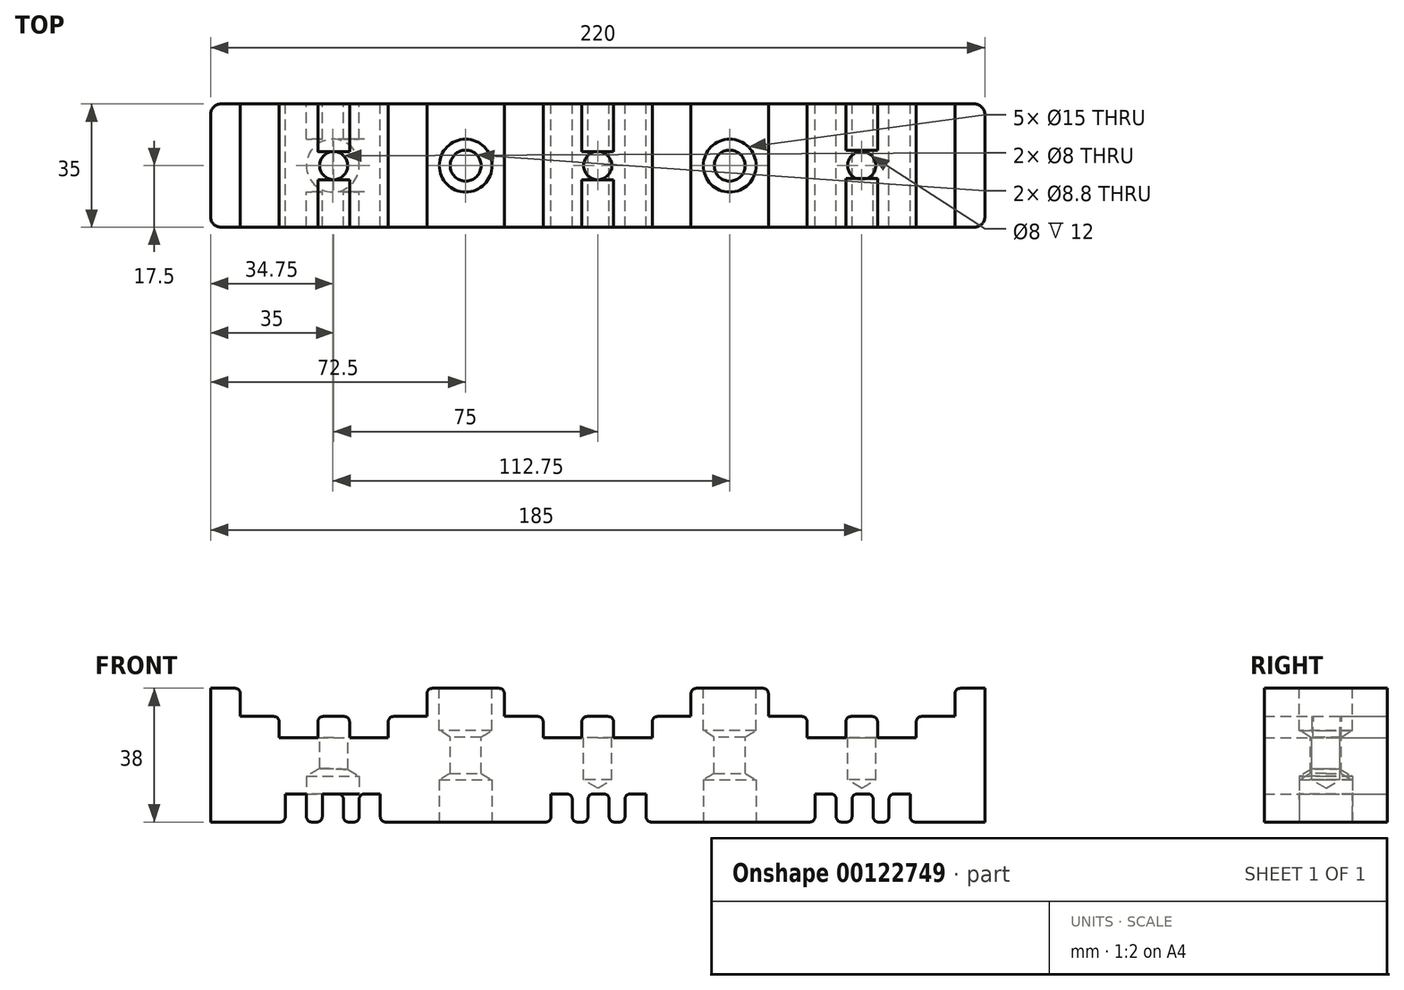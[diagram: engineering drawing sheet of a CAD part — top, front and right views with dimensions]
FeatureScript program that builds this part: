
annotation { "Feature Type Name" : "Feature", "Feature Type Description" : "" }
export const myFeature = defineFeature(function(context is Context, id is Id, definition is map)
    precondition{}
    {
        {
            var Q0;
            Q0=qCreatedBy(makeId("Front.planeOp"),FACE);
            var sketch = newSketch(context, id + "F0", { "sketchPlane" : qUnion([Q0])});
            skLineSegment(sketch, "E0.0", {"start": v(0.5, 5) * mm, "end": v(0.5, 11) * mm});
            skLineSegment(sketch, "E1.0", {"start": v(-10.5, 5) * mm, "end": v(-10.5, 11) * mm});
            skLineSegment(sketch, "E2.0", {"start": v(-21.5, 11) * mm, "end": v(-21.5, 19) * mm});
            skLineSegment(sketch, "E3.MirrorCS", {"start": v(31.5, 11) * mm, "end": v(31.5, 19) * mm});
            skLineSegment(sketch, "E4.MirrorCS", {"start": v(9.5, 5) * mm, "end": v(9.5, 11) * mm});
            skLineSegment(sketch, "E5.MirrorCS", {"start": v(20.5, 5) * mm, "end": v(20.5, 11) * mm});
            skLineSegment(sketch, "E6.trimOffspring", {"start": v(-21.5, 19) * mm, "end": v(-43.5, 19) * mm});
            skLineSegment(sketch, "E7.trimOffspring", {"start": v(0.5, 11) * mm, "end": v(9.5, 11) * mm});
            skLineSegment(sketch, "E8.trimOffspring", {"start": v(20.5, 11) * mm, "end": v(31.5, 11) * mm});
            skLineSegment(sketch, "E9.trimOffspring", {"start": v(-10.5, 5) * mm, "end": v(0.5, 5) * mm});
            skLineSegment(sketch, "E10.trimOffspring", {"start": v(-21.5, 11) * mm, "end": v(-10.5, 11) * mm});
            skLineSegment(sketch, "E11.trimOffspring", {"start": v(9.5, 5) * mm, "end": v(20.5, 5) * mm});
            skLineSegment(sketch, "E12.trimOffspring", {"start": v(53.5, 19) * mm, "end": v(31.5, 19) * mm});
            skLineSegment(sketch, "E13.trimOffspring", {"start": v(-8.25, -19) * mm, "end": v(-56.75, -19) * mm});
            skLineSegment(sketch, "E14.MirrorCS", {"start": v(-62.75, -19) * mm, "end": v(-62.75, -11) * mm});
            skLineSegment(sketch, "E15.MirrorCS", {"start": v(-67.25, -19) * mm, "end": v(-67.25, -11) * mm});
            skLineSegment(sketch, "E16.MirrorCS", {"start": v(-56.75, -19) * mm, "end": v(-56.75, -11) * mm});
            skLineSegment(sketch, "E17.MirrorCS", {"start": v(-67.25, -19) * mm, "end": v(-62.75, -19) * mm});
            skLineSegment(sketch, "E18.trimOffspring", {"start": v(-62.75, -11) * mm, "end": v(-56.75, -11) * mm});
            skLineSegment(sketch, "E19.trimOffspring", {"start": v(-62.75, -19) * mm, "end": v(-67.25, -19) * mm});
            skLineSegment(sketch, "E20", {"start": v(-73.25, -11) * mm, "end": v(-67.25, -11) * mm});
            skLineSegment(sketch, "E21.MirrorCS", {"start": v(-54.5, 5) * mm, "end": v(-54.5, 11) * mm});
            skLineSegment(sketch, "E22.MirrorCS", {"start": v(-43.5, 11) * mm, "end": v(-43.5, 19) * mm});
            skLineSegment(sketch, "E23.MirrorCS", {"start": v(-65.5, 11) * mm, "end": v(-74.5, 11) * mm});
            skLineSegment(sketch, "E24.MirrorCS", {"start": v(-54.5, 5) * mm, "end": v(-65.5, 5) * mm});
            skLineSegment(sketch, "E25.MirrorCS", {"start": v(-65.5, 5) * mm, "end": v(-65.5, 11) * mm});
            skLineSegment(sketch, "E26.MirrorCS", {"start": v(-96.5, 11) * mm, "end": v(-96.5, 19) * mm});
            skLineSegment(sketch, "E27.MirrorCS", {"start": v(-74.5, 5) * mm, "end": v(-74.5, 11) * mm});
            skLineSegment(sketch, "E28.MirrorCS", {"start": v(-85.5, 11) * mm, "end": v(-96.5, 11) * mm});
            skLineSegment(sketch, "E29.MirrorCS", {"start": v(-74.5, 5) * mm, "end": v(-85.5, 5) * mm});
            skLineSegment(sketch, "E30.MirrorCS", {"start": v(-85.5, 5) * mm, "end": v(-85.5, 11) * mm});
            skLineSegment(sketch, "E31.MirrorCS", {"start": v(-43.5, 11) * mm, "end": v(-54.5, 11) * mm});
            skLineSegment(sketch, "E32", {"start": v(-105, 19) * mm, "end": v(-105, -19) * mm});
            skLineSegment(sketch, "E33", {"start": v(-96.5, 19) * mm, "end": v(-105, 19) * mm});
            skLineSegment(sketch, "E34.MirrorCS", {"start": v(-73.25, -19) * mm, "end": v(-77.75, -19) * mm});
            skLineSegment(sketch, "E35.MirrorCS", {"start": v(-73.25, -19) * mm, "end": v(-73.25, -11) * mm});
            skLineSegment(sketch, "E36.MirrorCS", {"start": v(-83.75, -19) * mm, "end": v(-83.75, -11) * mm});
            skLineSegment(sketch, "E37.MirrorCS", {"start": v(-77.75, -19) * mm, "end": v(-73.25, -19) * mm});
            skLineSegment(sketch, "E38.MirrorCS", {"start": v(-77.75, -19) * mm, "end": v(-77.75, -11) * mm});
            skLineSegment(sketch, "E39.MirrorCS", {"start": v(-77.75, -11) * mm, "end": v(-83.75, -11) * mm});
            skLineSegment(sketch, "E40", {"start": v(-83.75, -19) * mm, "end": v(-105, -19) * mm});
            skLineSegment(sketch, "E41.MirrorCS", {"start": v(84.5, 11) * mm, "end": v(75.5, 11) * mm});
            skLineSegment(sketch, "E42.MirrorCS", {"start": v(95.5, 5) * mm, "end": v(84.5, 5) * mm});
            skLineSegment(sketch, "E43.MirrorCS", {"start": v(106.5, 11) * mm, "end": v(106.5, 19) * mm});
            skLineSegment(sketch, "E44.MirrorCS", {"start": v(95.5, 5) * mm, "end": v(95.5, 11) * mm});
            skLineSegment(sketch, "E45.MirrorCS", {"start": v(84.5, 5) * mm, "end": v(84.5, 11) * mm});
            skLineSegment(sketch, "E46.MirrorCS", {"start": v(64.5, 11) * mm, "end": v(53.5, 11) * mm});
            skLineSegment(sketch, "E47.MirrorCS", {"start": v(75.5, 5) * mm, "end": v(75.5, 11) * mm});
            skLineSegment(sketch, "E48.MirrorCS", {"start": v(64.5, 5) * mm, "end": v(64.5, 11) * mm});
            skLineSegment(sketch, "E49.MirrorCS", {"start": v(106.5, 11) * mm, "end": v(95.5, 11) * mm});
            skLineSegment(sketch, "E50.MirrorCS", {"start": v(53.5, 11) * mm, "end": v(53.5, 19) * mm});
            skLineSegment(sketch, "E51.MirrorCS", {"start": v(75.5, 5) * mm, "end": v(64.5, 5) * mm});
            skLineSegment(sketch, "E52.MirrorCS", {"start": v(72.75, -19) * mm, "end": v(77.25, -19) * mm});
            skLineSegment(sketch, "E53.MirrorCS", {"start": v(87.75, -19) * mm, "end": v(83.25, -19) * mm});
            skLineSegment(sketch, "E54.MirrorCS", {"start": v(83.25, -19) * mm, "end": v(87.75, -19) * mm});
            skLineSegment(sketch, "E55.MirrorCS", {"start": v(77.25, -19) * mm, "end": v(72.75, -19) * mm});
            skLineSegment(sketch, "E56.MirrorCS", {"start": v(93.75, -19) * mm, "end": v(93.75, -11) * mm});
            skLineSegment(sketch, "E57.MirrorCS", {"start": v(87.75, -19) * mm, "end": v(87.75, -11) * mm});
            skLineSegment(sketch, "E58.MirrorCS", {"start": v(77.25, -19) * mm, "end": v(77.25, -11) * mm});
            skLineSegment(sketch, "E59.MirrorCS", {"start": v(83.25, -11) * mm, "end": v(77.25, -11) * mm});
            skLineSegment(sketch, "E60.MirrorCS", {"start": v(72.75, -19) * mm, "end": v(72.75, -11) * mm});
            skLineSegment(sketch, "E61.MirrorCS", {"start": v(83.25, -19) * mm, "end": v(83.25, -11) * mm});
            skLineSegment(sketch, "E62.MirrorCS", {"start": v(66.75, -19) * mm, "end": v(66.75, -11) * mm});
            skLineSegment(sketch, "E63.MirrorCS", {"start": v(87.75, -11) * mm, "end": v(93.75, -11) * mm});
            skLineSegment(sketch, "E64.MirrorCS", {"start": v(18.25, -19) * mm, "end": v(66.75, -19) * mm});
            skLineSegment(sketch, "E65.MirrorCS", {"start": v(72.75, -11) * mm, "end": v(66.75, -11) * mm});
            skLineSegment(sketch, "E66.MirrorCS", {"start": v(115, 19) * mm, "end": v(115, -19) * mm});
            skLineSegment(sketch, "E67.MirrorCS", {"start": v(93.75, -19) * mm, "end": v(115, -19) * mm});
            skLineSegment(sketch, "E68.MirrorCS", {"start": v(106.5, 19) * mm, "end": v(115, 19) * mm});
            skLineSegment(sketch, "E69.MirrorCS", {"start": v(-2.25, -19) * mm, "end": v(2.25, -19) * mm});
            skLineSegment(sketch, "E70.MirrorCS", {"start": v(12.75, -19) * mm, "end": v(8.25, -19) * mm});
            skLineSegment(sketch, "E71.MirrorCS", {"start": v(2.25, -19) * mm, "end": v(-2.25, -19) * mm});
            skLineSegment(sketch, "E72.MirrorCS", {"start": v(8.25, -19) * mm, "end": v(12.75, -19) * mm});
            skLineSegment(sketch, "E73.MirrorCS", {"start": v(8.25, -11) * mm, "end": v(2.25, -11) * mm});
            skLineSegment(sketch, "E74.MirrorCS", {"start": v(-8.25, -19) * mm, "end": v(-8.25, -11) * mm});
            skLineSegment(sketch, "E75.MirrorCS", {"start": v(8.25, -19) * mm, "end": v(8.25, -11) * mm});
            skLineSegment(sketch, "E76.MirrorCS", {"start": v(2.25, -19) * mm, "end": v(2.25, -11) * mm});
            skLineSegment(sketch, "E77.MirrorCS", {"start": v(12.75, -19) * mm, "end": v(12.75, -11) * mm});
            skLineSegment(sketch, "E78.MirrorCS", {"start": v(-2.25, -19) * mm, "end": v(-2.25, -11) * mm});
            skLineSegment(sketch, "E79.MirrorCS", {"start": v(18.75, -19) * mm, "end": v(18.75, -11) * mm});
            skLineSegment(sketch, "E80.MirrorCS", {"start": v(-2.25, -11) * mm, "end": v(-8.25, -11) * mm});
            skLineSegment(sketch, "E81.MirrorCS", {"start": v(12.75, -11) * mm, "end": v(18.75, -11) * mm});
            skSolve(sketch);
        }
        {
            var Q0;
            Q0=makeQuery(id+"F0.imprint","IMPRINT",FACE,{"disambiguationData":[TD([[makeQuery(id+"F0.imprint","IMPRINT",EDGE,{"derivedFrom":sQuery(id+"F0.wireOp",EDGE,"qUKRLOlY-Y813-XrE7-N2OE-LMD0eoN4ccjQ.bottom")}),1.0]])]});
            var Q1;
            Q1=makeQuery(id+"F0.imprint","IMPRINT",FACE,{"disambiguationData":[TD([[makeQuery(id+"F0.imprint","IMPRINT",EDGE,{"derivedFrom":sQuery(id+"F0.wireOp",EDGE,"E0.0")}),-1.0]])]});
            extrude(context, id + "F1", {"entities" : qUnion([Q0, Q1]), "endBound" : BoundingType.SYMMETRIC, "depth" : 35 * mm});
        }
        {
            var Q0;
            Q0=makeQuery(id+"F1.opExtrude","SWEPT_FACE",FACE,{"disambiguationData":[OSD([sQuery(id+"F0.wireOp",EDGE,"E6.trimOffspring")])]});
            var sketch = newSketch(context, id + "F2", { "sketchPlane" : qUnion([Q0])});
            skPoint(sketch, "E82", {"position": v(-32.5, 0) * mm});
            skSolve(sketch);
        }
        {
            var Q0;
            Q0=makeQuery(id+"F1.opExtrude","SWEPT_FACE",FACE,{"disambiguationData":[OSD([sQuery(id+"F0.wireOp",EDGE,"E12.trimOffspring")])]});
            var sketch = newSketch(context, id + "F3", { "sketchPlane" : qUnion([Q0])});
            skPoint(sketch, "E83", {"position": v(42.5, 0) * mm});
            skSolve(sketch);
        }
        {
            var Q0;
            Q0=sQuery(id+"F2.wireOp",VERTEX,"E82");
            var Q1;
            Q1=sQuery(id+"F3.wireOp",VERTEX,"E83");
            var Q2;
            Q2=makeQuery(id+"F1.opExtrude","SWEPT_BODY",BODY,{"disambiguationData":[OSD([sQuery(id+"F0.wireOp",EDGE,"qUKRLOlY-Y813-XrE7-N2OE-LMD0eoN4ccjQ.bottom"),sQuery(id+"F0.wireOp",EDGE,"qUKRLOlY-Y813-XrE7-N2OE-LMD0eoN4ccjQ.top"),sQuery(id+"F0.wireOp",EDGE,"qUKRLOlY-Y813-XrE7-N2OE-LMD0eoN4ccjQ.left"),sQuery(id+"F0.wireOp",EDGE,"qUKRLOlY-Y813-XrE7-N2OE-LMD0eoN4ccjQ.right"),sQuery(id+"F0.wireOp",EDGE,"E0.0"),sQuery(id+"F0.wireOp",EDGE,"E1.0"),sQuery(id+"F0.wireOp",EDGE,"E2.0"),sQuery(id+"F0.wireOp",EDGE,"E3.MirrorCS"),sQuery(id+"F0.wireOp",EDGE,"E4.MirrorCS"),sQuery(id+"F0.wireOp",EDGE,"E5.MirrorCS"),sQuery(id+"F0.wireOp",EDGE,"TjQb5iGG-fkCj-vYVZ-Nu9b-291HRNzRSE6Z"),sQuery(id+"F0.wireOp",EDGE,"h24EoQMx-XsVo-RRqw-633f-RRsx9g0fc5Eq"),sQuery(id+"F0.wireOp",EDGE,"E6.trimOffspring"),sQuery(id+"F0.wireOp",EDGE,"E7.trimOffspring"),sQuery(id+"F0.wireOp",EDGE,"E8.trimOffspring"),sQuery(id+"F0.wireOp",EDGE,"8b73c36c-5120-4386-843b-b878e4734d4d1.MirrorCS"),sQuery(id+"F0.wireOp",EDGE,"8b73c36c-5120-4386-843b-b878e4734d4d3.MirrorCS"),sQuery(id+"F0.wireOp",EDGE,"8b73c36c-5120-4386-843b-b878e4734d4d4.MirrorCS"),sQuery(id+"F0.wireOp",EDGE,"8b73c36c-5120-4386-843b-b878e4734d4d5.MirrorCS"),sQuery(id+"F0.wireOp",EDGE,"8b73c36c-5120-4386-843b-b878e4734d4d7.MirrorCS"),sQuery(id+"F0.wireOp",EDGE,"8b73c36c-5120-4386-843b-b878e4734d4d8.MirrorCS"),sQuery(id+"F0.wireOp",EDGE,"65cf6d62-715c-4288-bebc-f9a01cc2506c2.MirrorCS"),sQuery(id+"F0.wireOp",EDGE,"65cf6d62-715c-4288-bebc-f9a01cc2506c3.MirrorCS"),sQuery(id+"F0.wireOp",EDGE,"65cf6d62-715c-4288-bebc-f9a01cc2506c4.MirrorCS"),sQuery(id+"F0.wireOp",EDGE,"65cf6d62-715c-4288-bebc-f9a01cc2506c5.MirrorCS"),sQuery(id+"F0.wireOp",EDGE,"65cf6d62-715c-4288-bebc-f9a01cc2506c6.MirrorCS"),sQuery(id+"F0.wireOp",EDGE,"65cf6d62-715c-4288-bebc-f9a01cc2506c7.MirrorCS"),sQuery(id+"F0.wireOp",EDGE,"4a5b6571-950c-4346-9e1a-99945dc3ca6b.trimOffspring"),sQuery(id+"F0.wireOp",EDGE,"fb7405d8-da36-487f-9ed8-d8622c99c7ee.trimOffspring"),sQuery(id+"F0.wireOp",EDGE,"ab254f91-2f6a-413b-b511-45bfff14a4ab.trimOffspring"),sQuery(id+"F0.wireOp",EDGE,"E9.trimOffspring"),sQuery(id+"F0.wireOp",EDGE,"E10.trimOffspring"),sQuery(id+"F0.wireOp",EDGE,"ce79941b-d8fd-4083-a2b9-c43c18c97298.trimOffspring"),sQuery(id+"F0.wireOp",EDGE,"E11.trimOffspring"),sQuery(id+"F0.wireOp",EDGE,"f32119e2-eb2d-4ad9-8c31-14fa2610f7e9.trimOffspring"),sQuery(id+"F0.wireOp",EDGE,"637628f6-76f3-4957-be79-8dbfd713e1ae.trimOffspring"),sQuery(id+"F0.wireOp",EDGE,"9485339e-7a65-4967-b426-d082cf6546cb.trimOffspring"),sQuery(id+"F0.wireOp",EDGE,"E12.trimOffspring"),sQuery(id+"F0.wireOp",EDGE,"f8046593-27ad-4778-b1d2-df4c1e0aed3c.trimOffspring"),sQuery(id+"F0.wireOp",EDGE,"d27bffa6-3cba-47ef-9795-798ee1ffffde.trimOffspring"),sQuery(id+"F0.wireOp",EDGE,"33a094fa-06ee-4256-bd1e-0f0ed5d178c0.0"),sQuery(id+"F0.wireOp",EDGE,"55134d35-60a4-4e31-8a7f-2c045abbdfaa.0"),sQuery(id+"F0.wireOp",EDGE,"4c2b0ad7-626b-4ce9-a313-3830519edc45.0"),sQuery(id+"F0.wireOp",EDGE,"3a7a6e12-f6d4-474c-8dc6-5767f96f3bfd0.MirrorCS"),sQuery(id+"F0.wireOp",EDGE,"f48c8ded-54f3-4706-a0ea-63bda03a67b5.trimOffspring"),sQuery(id+"F0.wireOp",EDGE,"E13.trimOffspring"),sQuery(id+"F0.wireOp",EDGE,"5ea96fcb-b208-4deb-8b26-572a86056be7.trimOffspring"),sQuery(id+"F0.wireOp",EDGE,"E16.MirrorCS"),sQuery(id+"F0.wireOp",EDGE,"E14.MirrorCS"),sQuery(id+"F0.wireOp",EDGE,"bcb0f907-a76e-4cdd-baca-5b1385e896aa2.MirrorCS"),sQuery(id+"F0.wireOp",EDGE,"E15.MirrorCS"),sQuery(id+"F0.wireOp",EDGE,"f6293f27-9fd1-40ac-aa67-5afb52735e2d0.MirrorCS"),sQuery(id+"F0.wireOp",EDGE,"f6293f27-9fd1-40ac-aa67-5afb52735e2d1.MirrorCS"),sQuery(id+"F0.wireOp",EDGE,"f6293f27-9fd1-40ac-aa67-5afb52735e2d3.MirrorCS"),sQuery(id+"F0.wireOp",EDGE,"f6293f27-9fd1-40ac-aa67-5afb52735e2d4.MirrorCS"),sQuery(id+"F0.wireOp",EDGE,"E18.trimOffspring"),sQuery(id+"F0.wireOp",EDGE,"E19.trimOffspring"),sQuery(id+"F0.wireOp",EDGE,"32ee123d-ca43-4cc0-928d-7201b603e702.trimOffspring"),sQuery(id+"F0.wireOp",EDGE,"E20"),sQuery(id+"F0.wireOp",EDGE,"5dcb935a-820c-4198-b4b2-0413f3b87393.trimOffspring"),sQuery(id+"F0.wireOp",EDGE,"7ee461ee-1d67-4faf-a147-f0287e78c71f.trimOffspring"),sQuery(id+"F0.wireOp",EDGE,"189ced0a-a9e9-466e-9166-4b62e1055adb.trimOffspring"),sQuery(id+"F0.wireOp",EDGE,"068751d8-bdd8-45ca-a637-cfe0f5a2bb4a.trimOffspring"),sQuery(id+"F0.wireOp",EDGE,"a825891d-b700-4e83-942a-2eee88b86e3d.trimOffspring")])]});
            hole(context, id + "F4", {"style" : HoleStyle.SIMPLE, "endStyle" : HoleEndStyle.THROUGH, "standardTappedOrClearance" : lookupTablePath({ "standard" : "ISO", "fit" : "Normal", "size" : "M8", "type" : "Clearance" }), "standardBlindInLast" : lookupTablePath({ "fit" : "Standard", "standard" : "ISO", "size" : "M8", "type" : "Clearance" }), "holeDiameter" : 8.8 * mm, "startFromSketch" : true, "locations" : qUnion([Q0, Q1]), "scope" : qUnion([Q2]), "isTappedThrough" : true});
        }
        {
            var Q0;
            Q0=makeQuery(id+"F1.opExtrude","SWEPT_FACE",FACE,{"disambiguationData":[OSD([sQuery(id+"F0.wireOp",EDGE,"E6.trimOffspring")])]});
            var sketch = newSketch(context, id + "F5", { "sketchPlane" : qUnion([Q0])});
            skPoint(sketch, "E84", {"position": v(-32.5, 0) * mm});
            skSolve(sketch);
        }
        {
            var Q0;
            Q0=makeQuery(id+"F1.opExtrude","SWEPT_FACE",FACE,{"disambiguationData":[OSD([sQuery(id+"F0.wireOp",EDGE,"E12.trimOffspring")])]});
            var sketch = newSketch(context, id + "F6", { "sketchPlane" : qUnion([Q0])});
            skPoint(sketch, "E85", {"position": v(42.5, 0) * mm});
            skSolve(sketch);
        }
        {
            var Q0;
            Q0=sQuery(id+"F5.wireOp",VERTEX,"E84");
            var Q1;
            Q1=makeQuery(id+"F1.opExtrude","SWEPT_BODY",BODY,{"disambiguationData":[OSD([sQuery(id+"F0.wireOp",EDGE,"qUKRLOlY-Y813-XrE7-N2OE-LMD0eoN4ccjQ.bottom"),sQuery(id+"F0.wireOp",EDGE,"qUKRLOlY-Y813-XrE7-N2OE-LMD0eoN4ccjQ.top"),sQuery(id+"F0.wireOp",EDGE,"qUKRLOlY-Y813-XrE7-N2OE-LMD0eoN4ccjQ.left"),sQuery(id+"F0.wireOp",EDGE,"qUKRLOlY-Y813-XrE7-N2OE-LMD0eoN4ccjQ.right"),sQuery(id+"F0.wireOp",EDGE,"E0.0"),sQuery(id+"F0.wireOp",EDGE,"E1.0"),sQuery(id+"F0.wireOp",EDGE,"E2.0"),sQuery(id+"F0.wireOp",EDGE,"E3.MirrorCS"),sQuery(id+"F0.wireOp",EDGE,"E4.MirrorCS"),sQuery(id+"F0.wireOp",EDGE,"E5.MirrorCS"),sQuery(id+"F0.wireOp",EDGE,"TjQb5iGG-fkCj-vYVZ-Nu9b-291HRNzRSE6Z"),sQuery(id+"F0.wireOp",EDGE,"h24EoQMx-XsVo-RRqw-633f-RRsx9g0fc5Eq"),sQuery(id+"F0.wireOp",EDGE,"E6.trimOffspring"),sQuery(id+"F0.wireOp",EDGE,"E7.trimOffspring"),sQuery(id+"F0.wireOp",EDGE,"E8.trimOffspring"),sQuery(id+"F0.wireOp",EDGE,"8b73c36c-5120-4386-843b-b878e4734d4d1.MirrorCS"),sQuery(id+"F0.wireOp",EDGE,"8b73c36c-5120-4386-843b-b878e4734d4d3.MirrorCS"),sQuery(id+"F0.wireOp",EDGE,"8b73c36c-5120-4386-843b-b878e4734d4d4.MirrorCS"),sQuery(id+"F0.wireOp",EDGE,"8b73c36c-5120-4386-843b-b878e4734d4d5.MirrorCS"),sQuery(id+"F0.wireOp",EDGE,"8b73c36c-5120-4386-843b-b878e4734d4d7.MirrorCS"),sQuery(id+"F0.wireOp",EDGE,"8b73c36c-5120-4386-843b-b878e4734d4d8.MirrorCS"),sQuery(id+"F0.wireOp",EDGE,"65cf6d62-715c-4288-bebc-f9a01cc2506c2.MirrorCS"),sQuery(id+"F0.wireOp",EDGE,"65cf6d62-715c-4288-bebc-f9a01cc2506c3.MirrorCS"),sQuery(id+"F0.wireOp",EDGE,"65cf6d62-715c-4288-bebc-f9a01cc2506c4.MirrorCS"),sQuery(id+"F0.wireOp",EDGE,"65cf6d62-715c-4288-bebc-f9a01cc2506c5.MirrorCS"),sQuery(id+"F0.wireOp",EDGE,"65cf6d62-715c-4288-bebc-f9a01cc2506c6.MirrorCS"),sQuery(id+"F0.wireOp",EDGE,"65cf6d62-715c-4288-bebc-f9a01cc2506c7.MirrorCS"),sQuery(id+"F0.wireOp",EDGE,"4a5b6571-950c-4346-9e1a-99945dc3ca6b.trimOffspring"),sQuery(id+"F0.wireOp",EDGE,"fb7405d8-da36-487f-9ed8-d8622c99c7ee.trimOffspring"),sQuery(id+"F0.wireOp",EDGE,"ab254f91-2f6a-413b-b511-45bfff14a4ab.trimOffspring"),sQuery(id+"F0.wireOp",EDGE,"E9.trimOffspring"),sQuery(id+"F0.wireOp",EDGE,"E10.trimOffspring"),sQuery(id+"F0.wireOp",EDGE,"ce79941b-d8fd-4083-a2b9-c43c18c97298.trimOffspring"),sQuery(id+"F0.wireOp",EDGE,"E11.trimOffspring"),sQuery(id+"F0.wireOp",EDGE,"f32119e2-eb2d-4ad9-8c31-14fa2610f7e9.trimOffspring"),sQuery(id+"F0.wireOp",EDGE,"637628f6-76f3-4957-be79-8dbfd713e1ae.trimOffspring"),sQuery(id+"F0.wireOp",EDGE,"9485339e-7a65-4967-b426-d082cf6546cb.trimOffspring"),sQuery(id+"F0.wireOp",EDGE,"E12.trimOffspring"),sQuery(id+"F0.wireOp",EDGE,"f8046593-27ad-4778-b1d2-df4c1e0aed3c.trimOffspring"),sQuery(id+"F0.wireOp",EDGE,"d27bffa6-3cba-47ef-9795-798ee1ffffde.trimOffspring"),sQuery(id+"F0.wireOp",EDGE,"33a094fa-06ee-4256-bd1e-0f0ed5d178c0.0"),sQuery(id+"F0.wireOp",EDGE,"55134d35-60a4-4e31-8a7f-2c045abbdfaa.0"),sQuery(id+"F0.wireOp",EDGE,"4c2b0ad7-626b-4ce9-a313-3830519edc45.0"),sQuery(id+"F0.wireOp",EDGE,"3a7a6e12-f6d4-474c-8dc6-5767f96f3bfd0.MirrorCS"),sQuery(id+"F0.wireOp",EDGE,"f48c8ded-54f3-4706-a0ea-63bda03a67b5.trimOffspring"),sQuery(id+"F0.wireOp",EDGE,"E13.trimOffspring"),sQuery(id+"F0.wireOp",EDGE,"5ea96fcb-b208-4deb-8b26-572a86056be7.trimOffspring"),sQuery(id+"F0.wireOp",EDGE,"E16.MirrorCS"),sQuery(id+"F0.wireOp",EDGE,"E14.MirrorCS"),sQuery(id+"F0.wireOp",EDGE,"bcb0f907-a76e-4cdd-baca-5b1385e896aa2.MirrorCS"),sQuery(id+"F0.wireOp",EDGE,"E15.MirrorCS"),sQuery(id+"F0.wireOp",EDGE,"f6293f27-9fd1-40ac-aa67-5afb52735e2d0.MirrorCS"),sQuery(id+"F0.wireOp",EDGE,"f6293f27-9fd1-40ac-aa67-5afb52735e2d1.MirrorCS"),sQuery(id+"F0.wireOp",EDGE,"f6293f27-9fd1-40ac-aa67-5afb52735e2d3.MirrorCS"),sQuery(id+"F0.wireOp",EDGE,"f6293f27-9fd1-40ac-aa67-5afb52735e2d4.MirrorCS"),sQuery(id+"F0.wireOp",EDGE,"E18.trimOffspring"),sQuery(id+"F0.wireOp",EDGE,"E19.trimOffspring"),sQuery(id+"F0.wireOp",EDGE,"32ee123d-ca43-4cc0-928d-7201b603e702.trimOffspring"),sQuery(id+"F0.wireOp",EDGE,"E20"),sQuery(id+"F0.wireOp",EDGE,"5dcb935a-820c-4198-b4b2-0413f3b87393.trimOffspring"),sQuery(id+"F0.wireOp",EDGE,"7ee461ee-1d67-4faf-a147-f0287e78c71f.trimOffspring"),sQuery(id+"F0.wireOp",EDGE,"189ced0a-a9e9-466e-9166-4b62e1055adb.trimOffspring"),sQuery(id+"F0.wireOp",EDGE,"068751d8-bdd8-45ca-a637-cfe0f5a2bb4a.trimOffspring"),sQuery(id+"F0.wireOp",EDGE,"a825891d-b700-4e83-942a-2eee88b86e3d.trimOffspring")])]});
            hole(context, id + "F7", {"style" : HoleStyle.SIMPLE, "endStyle" : HoleEndStyle.BLIND, "holeDiameter" : 15 * mm, "holeDepth" : 12 * mm, "startFromSketch" : true, "locations" : qUnion([Q0]), "scope" : qUnion([Q1])});
        }
        {
            var Q0;
            Q0=sQuery(id+"F6.wireOp",VERTEX,"E85");
            var Q1;
            Q1=makeQuery(id+"F1.opExtrude","SWEPT_BODY",BODY,{"disambiguationData":[OSD([sQuery(id+"F0.wireOp",EDGE,"qUKRLOlY-Y813-XrE7-N2OE-LMD0eoN4ccjQ.bottom"),sQuery(id+"F0.wireOp",EDGE,"qUKRLOlY-Y813-XrE7-N2OE-LMD0eoN4ccjQ.top"),sQuery(id+"F0.wireOp",EDGE,"qUKRLOlY-Y813-XrE7-N2OE-LMD0eoN4ccjQ.left"),sQuery(id+"F0.wireOp",EDGE,"qUKRLOlY-Y813-XrE7-N2OE-LMD0eoN4ccjQ.right"),sQuery(id+"F0.wireOp",EDGE,"E0.0"),sQuery(id+"F0.wireOp",EDGE,"E1.0"),sQuery(id+"F0.wireOp",EDGE,"E2.0"),sQuery(id+"F0.wireOp",EDGE,"E3.MirrorCS"),sQuery(id+"F0.wireOp",EDGE,"E4.MirrorCS"),sQuery(id+"F0.wireOp",EDGE,"E5.MirrorCS"),sQuery(id+"F0.wireOp",EDGE,"TjQb5iGG-fkCj-vYVZ-Nu9b-291HRNzRSE6Z"),sQuery(id+"F0.wireOp",EDGE,"h24EoQMx-XsVo-RRqw-633f-RRsx9g0fc5Eq"),sQuery(id+"F0.wireOp",EDGE,"E6.trimOffspring"),sQuery(id+"F0.wireOp",EDGE,"E7.trimOffspring"),sQuery(id+"F0.wireOp",EDGE,"E8.trimOffspring"),sQuery(id+"F0.wireOp",EDGE,"8b73c36c-5120-4386-843b-b878e4734d4d1.MirrorCS"),sQuery(id+"F0.wireOp",EDGE,"8b73c36c-5120-4386-843b-b878e4734d4d3.MirrorCS"),sQuery(id+"F0.wireOp",EDGE,"8b73c36c-5120-4386-843b-b878e4734d4d4.MirrorCS"),sQuery(id+"F0.wireOp",EDGE,"8b73c36c-5120-4386-843b-b878e4734d4d5.MirrorCS"),sQuery(id+"F0.wireOp",EDGE,"8b73c36c-5120-4386-843b-b878e4734d4d7.MirrorCS"),sQuery(id+"F0.wireOp",EDGE,"8b73c36c-5120-4386-843b-b878e4734d4d8.MirrorCS"),sQuery(id+"F0.wireOp",EDGE,"65cf6d62-715c-4288-bebc-f9a01cc2506c2.MirrorCS"),sQuery(id+"F0.wireOp",EDGE,"65cf6d62-715c-4288-bebc-f9a01cc2506c3.MirrorCS"),sQuery(id+"F0.wireOp",EDGE,"65cf6d62-715c-4288-bebc-f9a01cc2506c4.MirrorCS"),sQuery(id+"F0.wireOp",EDGE,"65cf6d62-715c-4288-bebc-f9a01cc2506c5.MirrorCS"),sQuery(id+"F0.wireOp",EDGE,"65cf6d62-715c-4288-bebc-f9a01cc2506c6.MirrorCS"),sQuery(id+"F0.wireOp",EDGE,"65cf6d62-715c-4288-bebc-f9a01cc2506c7.MirrorCS"),sQuery(id+"F0.wireOp",EDGE,"4a5b6571-950c-4346-9e1a-99945dc3ca6b.trimOffspring"),sQuery(id+"F0.wireOp",EDGE,"fb7405d8-da36-487f-9ed8-d8622c99c7ee.trimOffspring"),sQuery(id+"F0.wireOp",EDGE,"ab254f91-2f6a-413b-b511-45bfff14a4ab.trimOffspring"),sQuery(id+"F0.wireOp",EDGE,"E9.trimOffspring"),sQuery(id+"F0.wireOp",EDGE,"E10.trimOffspring"),sQuery(id+"F0.wireOp",EDGE,"ce79941b-d8fd-4083-a2b9-c43c18c97298.trimOffspring"),sQuery(id+"F0.wireOp",EDGE,"E11.trimOffspring"),sQuery(id+"F0.wireOp",EDGE,"f32119e2-eb2d-4ad9-8c31-14fa2610f7e9.trimOffspring"),sQuery(id+"F0.wireOp",EDGE,"637628f6-76f3-4957-be79-8dbfd713e1ae.trimOffspring"),sQuery(id+"F0.wireOp",EDGE,"9485339e-7a65-4967-b426-d082cf6546cb.trimOffspring"),sQuery(id+"F0.wireOp",EDGE,"E12.trimOffspring"),sQuery(id+"F0.wireOp",EDGE,"f8046593-27ad-4778-b1d2-df4c1e0aed3c.trimOffspring"),sQuery(id+"F0.wireOp",EDGE,"d27bffa6-3cba-47ef-9795-798ee1ffffde.trimOffspring"),sQuery(id+"F0.wireOp",EDGE,"33a094fa-06ee-4256-bd1e-0f0ed5d178c0.0"),sQuery(id+"F0.wireOp",EDGE,"55134d35-60a4-4e31-8a7f-2c045abbdfaa.0"),sQuery(id+"F0.wireOp",EDGE,"4c2b0ad7-626b-4ce9-a313-3830519edc45.0"),sQuery(id+"F0.wireOp",EDGE,"3a7a6e12-f6d4-474c-8dc6-5767f96f3bfd0.MirrorCS"),sQuery(id+"F0.wireOp",EDGE,"f48c8ded-54f3-4706-a0ea-63bda03a67b5.trimOffspring"),sQuery(id+"F0.wireOp",EDGE,"E13.trimOffspring"),sQuery(id+"F0.wireOp",EDGE,"5ea96fcb-b208-4deb-8b26-572a86056be7.trimOffspring"),sQuery(id+"F0.wireOp",EDGE,"E16.MirrorCS"),sQuery(id+"F0.wireOp",EDGE,"E14.MirrorCS"),sQuery(id+"F0.wireOp",EDGE,"bcb0f907-a76e-4cdd-baca-5b1385e896aa2.MirrorCS"),sQuery(id+"F0.wireOp",EDGE,"E15.MirrorCS"),sQuery(id+"F0.wireOp",EDGE,"f6293f27-9fd1-40ac-aa67-5afb52735e2d0.MirrorCS"),sQuery(id+"F0.wireOp",EDGE,"f6293f27-9fd1-40ac-aa67-5afb52735e2d1.MirrorCS"),sQuery(id+"F0.wireOp",EDGE,"f6293f27-9fd1-40ac-aa67-5afb52735e2d3.MirrorCS"),sQuery(id+"F0.wireOp",EDGE,"f6293f27-9fd1-40ac-aa67-5afb52735e2d4.MirrorCS"),sQuery(id+"F0.wireOp",EDGE,"E18.trimOffspring"),sQuery(id+"F0.wireOp",EDGE,"E19.trimOffspring"),sQuery(id+"F0.wireOp",EDGE,"32ee123d-ca43-4cc0-928d-7201b603e702.trimOffspring"),sQuery(id+"F0.wireOp",EDGE,"E20"),sQuery(id+"F0.wireOp",EDGE,"5dcb935a-820c-4198-b4b2-0413f3b87393.trimOffspring"),sQuery(id+"F0.wireOp",EDGE,"7ee461ee-1d67-4faf-a147-f0287e78c71f.trimOffspring"),sQuery(id+"F0.wireOp",EDGE,"189ced0a-a9e9-466e-9166-4b62e1055adb.trimOffspring"),sQuery(id+"F0.wireOp",EDGE,"068751d8-bdd8-45ca-a637-cfe0f5a2bb4a.trimOffspring"),sQuery(id+"F0.wireOp",EDGE,"a825891d-b700-4e83-942a-2eee88b86e3d.trimOffspring")])]});
            hole(context, id + "F8", {"style" : HoleStyle.SIMPLE, "endStyle" : HoleEndStyle.BLIND, "holeDiameter" : 15 * mm, "holeDepth" : 12 * mm, "startFromSketch" : true, "locations" : qUnion([Q0]), "scope" : qUnion([Q1])});
        }
        {
            var Q0;
            Q0=makeQuery(id+"F1.opExtrude","SWEPT_FACE",FACE,{"disambiguationData":[OSD([sQuery(id+"F0.wireOp",EDGE,"E64.MirrorCS")])]});
            var sketch = newSketch(context, id + "F9", { "sketchPlane" : qUnion([Q0])});
            skPoint(sketch, "E86", {"position": v(42.5, 0) * mm});
            skSolve(sketch);
        }
        {
            var Q0;
            Q0=makeQuery(id+"F1.opExtrude","SWEPT_FACE",FACE,{"disambiguationData":[OSD([sQuery(id+"F0.wireOp",EDGE,"E13.trimOffspring")])]});
            var sketch = newSketch(context, id + "F10", { "sketchPlane" : qUnion([Q0])});
            skPoint(sketch, "E87", {"position": v(-32.5, 0) * mm});
            skSolve(sketch);
        }
        {
            var Q0;
            Q0=sQuery(id+"F9.wireOp",VERTEX,"E86");
            var Q1;
            Q1=makeQuery(id+"F1.opExtrude","SWEPT_BODY",BODY,{"disambiguationData":[OSD([sQuery(id+"F0.wireOp",EDGE,"qUKRLOlY-Y813-XrE7-N2OE-LMD0eoN4ccjQ.bottom"),sQuery(id+"F0.wireOp",EDGE,"qUKRLOlY-Y813-XrE7-N2OE-LMD0eoN4ccjQ.top"),sQuery(id+"F0.wireOp",EDGE,"qUKRLOlY-Y813-XrE7-N2OE-LMD0eoN4ccjQ.left"),sQuery(id+"F0.wireOp",EDGE,"qUKRLOlY-Y813-XrE7-N2OE-LMD0eoN4ccjQ.right"),sQuery(id+"F0.wireOp",EDGE,"E0.0"),sQuery(id+"F0.wireOp",EDGE,"E1.0"),sQuery(id+"F0.wireOp",EDGE,"E2.0"),sQuery(id+"F0.wireOp",EDGE,"E3.MirrorCS"),sQuery(id+"F0.wireOp",EDGE,"E4.MirrorCS"),sQuery(id+"F0.wireOp",EDGE,"E5.MirrorCS"),sQuery(id+"F0.wireOp",EDGE,"TjQb5iGG-fkCj-vYVZ-Nu9b-291HRNzRSE6Z"),sQuery(id+"F0.wireOp",EDGE,"h24EoQMx-XsVo-RRqw-633f-RRsx9g0fc5Eq"),sQuery(id+"F0.wireOp",EDGE,"E6.trimOffspring"),sQuery(id+"F0.wireOp",EDGE,"E7.trimOffspring"),sQuery(id+"F0.wireOp",EDGE,"E8.trimOffspring"),sQuery(id+"F0.wireOp",EDGE,"8b73c36c-5120-4386-843b-b878e4734d4d1.MirrorCS"),sQuery(id+"F0.wireOp",EDGE,"8b73c36c-5120-4386-843b-b878e4734d4d3.MirrorCS"),sQuery(id+"F0.wireOp",EDGE,"8b73c36c-5120-4386-843b-b878e4734d4d4.MirrorCS"),sQuery(id+"F0.wireOp",EDGE,"8b73c36c-5120-4386-843b-b878e4734d4d5.MirrorCS"),sQuery(id+"F0.wireOp",EDGE,"8b73c36c-5120-4386-843b-b878e4734d4d7.MirrorCS"),sQuery(id+"F0.wireOp",EDGE,"8b73c36c-5120-4386-843b-b878e4734d4d8.MirrorCS"),sQuery(id+"F0.wireOp",EDGE,"65cf6d62-715c-4288-bebc-f9a01cc2506c2.MirrorCS"),sQuery(id+"F0.wireOp",EDGE,"65cf6d62-715c-4288-bebc-f9a01cc2506c3.MirrorCS"),sQuery(id+"F0.wireOp",EDGE,"65cf6d62-715c-4288-bebc-f9a01cc2506c4.MirrorCS"),sQuery(id+"F0.wireOp",EDGE,"65cf6d62-715c-4288-bebc-f9a01cc2506c5.MirrorCS"),sQuery(id+"F0.wireOp",EDGE,"65cf6d62-715c-4288-bebc-f9a01cc2506c6.MirrorCS"),sQuery(id+"F0.wireOp",EDGE,"65cf6d62-715c-4288-bebc-f9a01cc2506c7.MirrorCS"),sQuery(id+"F0.wireOp",EDGE,"4a5b6571-950c-4346-9e1a-99945dc3ca6b.trimOffspring"),sQuery(id+"F0.wireOp",EDGE,"fb7405d8-da36-487f-9ed8-d8622c99c7ee.trimOffspring"),sQuery(id+"F0.wireOp",EDGE,"ab254f91-2f6a-413b-b511-45bfff14a4ab.trimOffspring"),sQuery(id+"F0.wireOp",EDGE,"E9.trimOffspring"),sQuery(id+"F0.wireOp",EDGE,"E10.trimOffspring"),sQuery(id+"F0.wireOp",EDGE,"ce79941b-d8fd-4083-a2b9-c43c18c97298.trimOffspring"),sQuery(id+"F0.wireOp",EDGE,"E11.trimOffspring"),sQuery(id+"F0.wireOp",EDGE,"f32119e2-eb2d-4ad9-8c31-14fa2610f7e9.trimOffspring"),sQuery(id+"F0.wireOp",EDGE,"637628f6-76f3-4957-be79-8dbfd713e1ae.trimOffspring"),sQuery(id+"F0.wireOp",EDGE,"9485339e-7a65-4967-b426-d082cf6546cb.trimOffspring"),sQuery(id+"F0.wireOp",EDGE,"E12.trimOffspring"),sQuery(id+"F0.wireOp",EDGE,"f8046593-27ad-4778-b1d2-df4c1e0aed3c.trimOffspring"),sQuery(id+"F0.wireOp",EDGE,"d27bffa6-3cba-47ef-9795-798ee1ffffde.trimOffspring"),sQuery(id+"F0.wireOp",EDGE,"33a094fa-06ee-4256-bd1e-0f0ed5d178c0.0"),sQuery(id+"F0.wireOp",EDGE,"55134d35-60a4-4e31-8a7f-2c045abbdfaa.0"),sQuery(id+"F0.wireOp",EDGE,"4c2b0ad7-626b-4ce9-a313-3830519edc45.0"),sQuery(id+"F0.wireOp",EDGE,"3a7a6e12-f6d4-474c-8dc6-5767f96f3bfd0.MirrorCS"),sQuery(id+"F0.wireOp",EDGE,"f48c8ded-54f3-4706-a0ea-63bda03a67b5.trimOffspring"),sQuery(id+"F0.wireOp",EDGE,"E13.trimOffspring"),sQuery(id+"F0.wireOp",EDGE,"5ea96fcb-b208-4deb-8b26-572a86056be7.trimOffspring"),sQuery(id+"F0.wireOp",EDGE,"E16.MirrorCS"),sQuery(id+"F0.wireOp",EDGE,"E14.MirrorCS"),sQuery(id+"F0.wireOp",EDGE,"bcb0f907-a76e-4cdd-baca-5b1385e896aa2.MirrorCS"),sQuery(id+"F0.wireOp",EDGE,"E15.MirrorCS"),sQuery(id+"F0.wireOp",EDGE,"f6293f27-9fd1-40ac-aa67-5afb52735e2d0.MirrorCS"),sQuery(id+"F0.wireOp",EDGE,"f6293f27-9fd1-40ac-aa67-5afb52735e2d1.MirrorCS"),sQuery(id+"F0.wireOp",EDGE,"f6293f27-9fd1-40ac-aa67-5afb52735e2d3.MirrorCS"),sQuery(id+"F0.wireOp",EDGE,"f6293f27-9fd1-40ac-aa67-5afb52735e2d4.MirrorCS"),sQuery(id+"F0.wireOp",EDGE,"E18.trimOffspring"),sQuery(id+"F0.wireOp",EDGE,"E19.trimOffspring"),sQuery(id+"F0.wireOp",EDGE,"32ee123d-ca43-4cc0-928d-7201b603e702.trimOffspring"),sQuery(id+"F0.wireOp",EDGE,"E20"),sQuery(id+"F0.wireOp",EDGE,"5dcb935a-820c-4198-b4b2-0413f3b87393.trimOffspring"),sQuery(id+"F0.wireOp",EDGE,"7ee461ee-1d67-4faf-a147-f0287e78c71f.trimOffspring"),sQuery(id+"F0.wireOp",EDGE,"189ced0a-a9e9-466e-9166-4b62e1055adb.trimOffspring"),sQuery(id+"F0.wireOp",EDGE,"068751d8-bdd8-45ca-a637-cfe0f5a2bb4a.trimOffspring"),sQuery(id+"F0.wireOp",EDGE,"a825891d-b700-4e83-942a-2eee88b86e3d.trimOffspring")])]});
            hole(context, id + "F11", {"style" : HoleStyle.SIMPLE, "endStyle" : HoleEndStyle.BLIND, "holeDiameter" : 15 * mm, "holeDepth" : 12 * mm, "startFromSketch" : true, "locations" : qUnion([Q0]), "scope" : qUnion([Q1])});
        }
        {
            var Q0;
            Q0=sQuery(id+"F10.wireOp",VERTEX,"E87");
            var Q1;
            Q1=makeQuery(id+"F1.opExtrude","SWEPT_BODY",BODY,{"disambiguationData":[OSD([sQuery(id+"F0.wireOp",EDGE,"qUKRLOlY-Y813-XrE7-N2OE-LMD0eoN4ccjQ.bottom"),sQuery(id+"F0.wireOp",EDGE,"qUKRLOlY-Y813-XrE7-N2OE-LMD0eoN4ccjQ.top"),sQuery(id+"F0.wireOp",EDGE,"qUKRLOlY-Y813-XrE7-N2OE-LMD0eoN4ccjQ.left"),sQuery(id+"F0.wireOp",EDGE,"qUKRLOlY-Y813-XrE7-N2OE-LMD0eoN4ccjQ.right"),sQuery(id+"F0.wireOp",EDGE,"E0.0"),sQuery(id+"F0.wireOp",EDGE,"E1.0"),sQuery(id+"F0.wireOp",EDGE,"E2.0"),sQuery(id+"F0.wireOp",EDGE,"E3.MirrorCS"),sQuery(id+"F0.wireOp",EDGE,"E4.MirrorCS"),sQuery(id+"F0.wireOp",EDGE,"E5.MirrorCS"),sQuery(id+"F0.wireOp",EDGE,"TjQb5iGG-fkCj-vYVZ-Nu9b-291HRNzRSE6Z"),sQuery(id+"F0.wireOp",EDGE,"h24EoQMx-XsVo-RRqw-633f-RRsx9g0fc5Eq"),sQuery(id+"F0.wireOp",EDGE,"E6.trimOffspring"),sQuery(id+"F0.wireOp",EDGE,"E7.trimOffspring"),sQuery(id+"F0.wireOp",EDGE,"E8.trimOffspring"),sQuery(id+"F0.wireOp",EDGE,"8b73c36c-5120-4386-843b-b878e4734d4d1.MirrorCS"),sQuery(id+"F0.wireOp",EDGE,"8b73c36c-5120-4386-843b-b878e4734d4d3.MirrorCS"),sQuery(id+"F0.wireOp",EDGE,"8b73c36c-5120-4386-843b-b878e4734d4d4.MirrorCS"),sQuery(id+"F0.wireOp",EDGE,"8b73c36c-5120-4386-843b-b878e4734d4d5.MirrorCS"),sQuery(id+"F0.wireOp",EDGE,"8b73c36c-5120-4386-843b-b878e4734d4d7.MirrorCS"),sQuery(id+"F0.wireOp",EDGE,"8b73c36c-5120-4386-843b-b878e4734d4d8.MirrorCS"),sQuery(id+"F0.wireOp",EDGE,"65cf6d62-715c-4288-bebc-f9a01cc2506c2.MirrorCS"),sQuery(id+"F0.wireOp",EDGE,"65cf6d62-715c-4288-bebc-f9a01cc2506c3.MirrorCS"),sQuery(id+"F0.wireOp",EDGE,"65cf6d62-715c-4288-bebc-f9a01cc2506c4.MirrorCS"),sQuery(id+"F0.wireOp",EDGE,"65cf6d62-715c-4288-bebc-f9a01cc2506c5.MirrorCS"),sQuery(id+"F0.wireOp",EDGE,"65cf6d62-715c-4288-bebc-f9a01cc2506c6.MirrorCS"),sQuery(id+"F0.wireOp",EDGE,"65cf6d62-715c-4288-bebc-f9a01cc2506c7.MirrorCS"),sQuery(id+"F0.wireOp",EDGE,"4a5b6571-950c-4346-9e1a-99945dc3ca6b.trimOffspring"),sQuery(id+"F0.wireOp",EDGE,"fb7405d8-da36-487f-9ed8-d8622c99c7ee.trimOffspring"),sQuery(id+"F0.wireOp",EDGE,"ab254f91-2f6a-413b-b511-45bfff14a4ab.trimOffspring"),sQuery(id+"F0.wireOp",EDGE,"E9.trimOffspring"),sQuery(id+"F0.wireOp",EDGE,"E10.trimOffspring"),sQuery(id+"F0.wireOp",EDGE,"ce79941b-d8fd-4083-a2b9-c43c18c97298.trimOffspring"),sQuery(id+"F0.wireOp",EDGE,"E11.trimOffspring"),sQuery(id+"F0.wireOp",EDGE,"f32119e2-eb2d-4ad9-8c31-14fa2610f7e9.trimOffspring"),sQuery(id+"F0.wireOp",EDGE,"637628f6-76f3-4957-be79-8dbfd713e1ae.trimOffspring"),sQuery(id+"F0.wireOp",EDGE,"9485339e-7a65-4967-b426-d082cf6546cb.trimOffspring"),sQuery(id+"F0.wireOp",EDGE,"E12.trimOffspring"),sQuery(id+"F0.wireOp",EDGE,"f8046593-27ad-4778-b1d2-df4c1e0aed3c.trimOffspring"),sQuery(id+"F0.wireOp",EDGE,"d27bffa6-3cba-47ef-9795-798ee1ffffde.trimOffspring"),sQuery(id+"F0.wireOp",EDGE,"33a094fa-06ee-4256-bd1e-0f0ed5d178c0.0"),sQuery(id+"F0.wireOp",EDGE,"55134d35-60a4-4e31-8a7f-2c045abbdfaa.0"),sQuery(id+"F0.wireOp",EDGE,"4c2b0ad7-626b-4ce9-a313-3830519edc45.0"),sQuery(id+"F0.wireOp",EDGE,"3a7a6e12-f6d4-474c-8dc6-5767f96f3bfd0.MirrorCS"),sQuery(id+"F0.wireOp",EDGE,"f48c8ded-54f3-4706-a0ea-63bda03a67b5.trimOffspring"),sQuery(id+"F0.wireOp",EDGE,"E13.trimOffspring"),sQuery(id+"F0.wireOp",EDGE,"5ea96fcb-b208-4deb-8b26-572a86056be7.trimOffspring"),sQuery(id+"F0.wireOp",EDGE,"E16.MirrorCS"),sQuery(id+"F0.wireOp",EDGE,"E14.MirrorCS"),sQuery(id+"F0.wireOp",EDGE,"bcb0f907-a76e-4cdd-baca-5b1385e896aa2.MirrorCS"),sQuery(id+"F0.wireOp",EDGE,"E15.MirrorCS"),sQuery(id+"F0.wireOp",EDGE,"f6293f27-9fd1-40ac-aa67-5afb52735e2d0.MirrorCS"),sQuery(id+"F0.wireOp",EDGE,"f6293f27-9fd1-40ac-aa67-5afb52735e2d1.MirrorCS"),sQuery(id+"F0.wireOp",EDGE,"f6293f27-9fd1-40ac-aa67-5afb52735e2d3.MirrorCS"),sQuery(id+"F0.wireOp",EDGE,"f6293f27-9fd1-40ac-aa67-5afb52735e2d4.MirrorCS"),sQuery(id+"F0.wireOp",EDGE,"E18.trimOffspring"),sQuery(id+"F0.wireOp",EDGE,"E19.trimOffspring"),sQuery(id+"F0.wireOp",EDGE,"32ee123d-ca43-4cc0-928d-7201b603e702.trimOffspring"),sQuery(id+"F0.wireOp",EDGE,"E20"),sQuery(id+"F0.wireOp",EDGE,"5dcb935a-820c-4198-b4b2-0413f3b87393.trimOffspring"),sQuery(id+"F0.wireOp",EDGE,"7ee461ee-1d67-4faf-a147-f0287e78c71f.trimOffspring"),sQuery(id+"F0.wireOp",EDGE,"189ced0a-a9e9-466e-9166-4b62e1055adb.trimOffspring"),sQuery(id+"F0.wireOp",EDGE,"068751d8-bdd8-45ca-a637-cfe0f5a2bb4a.trimOffspring"),sQuery(id+"F0.wireOp",EDGE,"a825891d-b700-4e83-942a-2eee88b86e3d.trimOffspring")])]});
            hole(context, id + "F12", {"style" : HoleStyle.SIMPLE, "endStyle" : HoleEndStyle.BLIND, "holeDiameter" : 15 * mm, "holeDepth" : 12 * mm, "startFromSketch" : true, "locations" : qUnion([Q0]), "scope" : qUnion([Q1])});
        }
        {
            var Q0;
            Q0=makeQuery(id+"F1.opExtrude","SWEPT_FACE",FACE,{"disambiguationData":[OSD([sQuery(id+"F0.wireOp",EDGE,"E7.trimOffspring")])]});
            var sketch = newSketch(context, id + "F13", { "sketchPlane" : qUnion([Q0])});
            skPoint(sketch, "E88", {"position": v(0, 0) * mm});
            skLineSegment(sketch, "E89.bottom", {"start": v(9.5, 4) * mm, "end": v(-9.5, 4) * mm});
            skLineSegment(sketch, "E89.top", {"start": v(9.5, -4) * mm, "end": v(-9.5, -4) * mm});
            skLineSegment(sketch, "E89.left", {"start": v(9.5, 4) * mm, "end": v(9.5, -4) * mm});
            skLineSegment(sketch, "E89.right", {"start": v(-9.5, 4) * mm, "end": v(-9.5, -4) * mm});
            skSolve(sketch);
        }
        {
            var Q0;
            Q0=makeQuery(id+"F13.imprint","IMPRINT",FACE,{"disambiguationData":[TD([[makeQuery(id+"F13.imprint","IMPRINT",EDGE,{"derivedFrom":sQuery(id+"F13.wireOp",EDGE,"E89.bottom")}),1.0]])]});
            extrude(context, id + "F14", {"entities" : qUnion([Q0]), "operationType" : NewBodyOperationType.REMOVE, "oppositeDirection" : true, "depth" : 6 * mm});
        }
        {
            var Q0;
            Q0=makeQuery(id+"F14.boolean.opBoolean","MERGE",FACE,{"derivedFrom":[makeQuery(id+"F1.opExtrude","SWEPT_FACE",FACE,{"disambiguationData":[OSD([sQuery(id+"F0.wireOp",EDGE,"E9.trimOffspring")])]}),makeQuery(id+"F1.opExtrude","SWEPT_FACE",FACE,{"disambiguationData":[OSD([sQuery(id+"F0.wireOp",EDGE,"E11.trimOffspring")])]}),makeQuery(id+"F14.opExtrude","CAP_FACE",FACE,{"disambiguationData":[OSD([sQuery(id+"F13.wireOp",EDGE,"E89.bottom"),sQuery(id+"F13.wireOp",EDGE,"E89.top"),sQuery(id+"F13.wireOp",EDGE,"E89.left"),sQuery(id+"F13.wireOp",EDGE,"E89.right")])],"isStart":false})]});
            var sketch = newSketch(context, id + "F15", { "sketchPlane" : qUnion([Q0])});
            skPoint(sketch, "E90", {"position": v(5, 0) * mm});
            skSolve(sketch);
        }
        {
            var Q0;
            Q0=sQuery(id+"F15.wireOp",VERTEX,"E90");
            var Q1;
            Q1=makeQuery(id+"F1.opExtrude","SWEPT_BODY",BODY,{"disambiguationData":[OSD([sQuery(id+"F0.wireOp",EDGE,"qUKRLOlY-Y813-XrE7-N2OE-LMD0eoN4ccjQ.bottom"),sQuery(id+"F0.wireOp",EDGE,"qUKRLOlY-Y813-XrE7-N2OE-LMD0eoN4ccjQ.top"),sQuery(id+"F0.wireOp",EDGE,"qUKRLOlY-Y813-XrE7-N2OE-LMD0eoN4ccjQ.left"),sQuery(id+"F0.wireOp",EDGE,"qUKRLOlY-Y813-XrE7-N2OE-LMD0eoN4ccjQ.right"),sQuery(id+"F0.wireOp",EDGE,"E0.0"),sQuery(id+"F0.wireOp",EDGE,"E1.0"),sQuery(id+"F0.wireOp",EDGE,"E2.0"),sQuery(id+"F0.wireOp",EDGE,"E3.MirrorCS"),sQuery(id+"F0.wireOp",EDGE,"E4.MirrorCS"),sQuery(id+"F0.wireOp",EDGE,"E5.MirrorCS"),sQuery(id+"F0.wireOp",EDGE,"TjQb5iGG-fkCj-vYVZ-Nu9b-291HRNzRSE6Z"),sQuery(id+"F0.wireOp",EDGE,"h24EoQMx-XsVo-RRqw-633f-RRsx9g0fc5Eq"),sQuery(id+"F0.wireOp",EDGE,"E6.trimOffspring"),sQuery(id+"F0.wireOp",EDGE,"E7.trimOffspring"),sQuery(id+"F0.wireOp",EDGE,"E8.trimOffspring"),sQuery(id+"F0.wireOp",EDGE,"8b73c36c-5120-4386-843b-b878e4734d4d1.MirrorCS"),sQuery(id+"F0.wireOp",EDGE,"8b73c36c-5120-4386-843b-b878e4734d4d3.MirrorCS"),sQuery(id+"F0.wireOp",EDGE,"8b73c36c-5120-4386-843b-b878e4734d4d4.MirrorCS"),sQuery(id+"F0.wireOp",EDGE,"8b73c36c-5120-4386-843b-b878e4734d4d5.MirrorCS"),sQuery(id+"F0.wireOp",EDGE,"8b73c36c-5120-4386-843b-b878e4734d4d7.MirrorCS"),sQuery(id+"F0.wireOp",EDGE,"8b73c36c-5120-4386-843b-b878e4734d4d8.MirrorCS"),sQuery(id+"F0.wireOp",EDGE,"65cf6d62-715c-4288-bebc-f9a01cc2506c2.MirrorCS"),sQuery(id+"F0.wireOp",EDGE,"65cf6d62-715c-4288-bebc-f9a01cc2506c3.MirrorCS"),sQuery(id+"F0.wireOp",EDGE,"65cf6d62-715c-4288-bebc-f9a01cc2506c4.MirrorCS"),sQuery(id+"F0.wireOp",EDGE,"65cf6d62-715c-4288-bebc-f9a01cc2506c5.MirrorCS"),sQuery(id+"F0.wireOp",EDGE,"65cf6d62-715c-4288-bebc-f9a01cc2506c6.MirrorCS"),sQuery(id+"F0.wireOp",EDGE,"65cf6d62-715c-4288-bebc-f9a01cc2506c7.MirrorCS"),sQuery(id+"F0.wireOp",EDGE,"4a5b6571-950c-4346-9e1a-99945dc3ca6b.trimOffspring"),sQuery(id+"F0.wireOp",EDGE,"fb7405d8-da36-487f-9ed8-d8622c99c7ee.trimOffspring"),sQuery(id+"F0.wireOp",EDGE,"ab254f91-2f6a-413b-b511-45bfff14a4ab.trimOffspring"),sQuery(id+"F0.wireOp",EDGE,"E9.trimOffspring"),sQuery(id+"F0.wireOp",EDGE,"E10.trimOffspring"),sQuery(id+"F0.wireOp",EDGE,"ce79941b-d8fd-4083-a2b9-c43c18c97298.trimOffspring"),sQuery(id+"F0.wireOp",EDGE,"E11.trimOffspring"),sQuery(id+"F0.wireOp",EDGE,"f32119e2-eb2d-4ad9-8c31-14fa2610f7e9.trimOffspring"),sQuery(id+"F0.wireOp",EDGE,"637628f6-76f3-4957-be79-8dbfd713e1ae.trimOffspring"),sQuery(id+"F0.wireOp",EDGE,"9485339e-7a65-4967-b426-d082cf6546cb.trimOffspring"),sQuery(id+"F0.wireOp",EDGE,"E12.trimOffspring"),sQuery(id+"F0.wireOp",EDGE,"f8046593-27ad-4778-b1d2-df4c1e0aed3c.trimOffspring"),sQuery(id+"F0.wireOp",EDGE,"d27bffa6-3cba-47ef-9795-798ee1ffffde.trimOffspring"),sQuery(id+"F0.wireOp",EDGE,"33a094fa-06ee-4256-bd1e-0f0ed5d178c0.0"),sQuery(id+"F0.wireOp",EDGE,"55134d35-60a4-4e31-8a7f-2c045abbdfaa.0"),sQuery(id+"F0.wireOp",EDGE,"4c2b0ad7-626b-4ce9-a313-3830519edc45.0"),sQuery(id+"F0.wireOp",EDGE,"3a7a6e12-f6d4-474c-8dc6-5767f96f3bfd0.MirrorCS"),sQuery(id+"F0.wireOp",EDGE,"f48c8ded-54f3-4706-a0ea-63bda03a67b5.trimOffspring"),sQuery(id+"F0.wireOp",EDGE,"E13.trimOffspring"),sQuery(id+"F0.wireOp",EDGE,"5ea96fcb-b208-4deb-8b26-572a86056be7.trimOffspring"),sQuery(id+"F0.wireOp",EDGE,"E16.MirrorCS"),sQuery(id+"F0.wireOp",EDGE,"E14.MirrorCS"),sQuery(id+"F0.wireOp",EDGE,"bcb0f907-a76e-4cdd-baca-5b1385e896aa2.MirrorCS"),sQuery(id+"F0.wireOp",EDGE,"E15.MirrorCS"),sQuery(id+"F0.wireOp",EDGE,"f6293f27-9fd1-40ac-aa67-5afb52735e2d0.MirrorCS"),sQuery(id+"F0.wireOp",EDGE,"f6293f27-9fd1-40ac-aa67-5afb52735e2d1.MirrorCS"),sQuery(id+"F0.wireOp",EDGE,"f6293f27-9fd1-40ac-aa67-5afb52735e2d3.MirrorCS"),sQuery(id+"F0.wireOp",EDGE,"f6293f27-9fd1-40ac-aa67-5afb52735e2d4.MirrorCS"),sQuery(id+"F0.wireOp",EDGE,"E18.trimOffspring"),sQuery(id+"F0.wireOp",EDGE,"E19.trimOffspring"),sQuery(id+"F0.wireOp",EDGE,"32ee123d-ca43-4cc0-928d-7201b603e702.trimOffspring"),sQuery(id+"F0.wireOp",EDGE,"E20"),sQuery(id+"F0.wireOp",EDGE,"5dcb935a-820c-4198-b4b2-0413f3b87393.trimOffspring"),sQuery(id+"F0.wireOp",EDGE,"7ee461ee-1d67-4faf-a147-f0287e78c71f.trimOffspring"),sQuery(id+"F0.wireOp",EDGE,"189ced0a-a9e9-466e-9166-4b62e1055adb.trimOffspring"),sQuery(id+"F0.wireOp",EDGE,"068751d8-bdd8-45ca-a637-cfe0f5a2bb4a.trimOffspring"),sQuery(id+"F0.wireOp",EDGE,"a825891d-b700-4e83-942a-2eee88b86e3d.trimOffspring")])]});
            hole(context, id + "F16", {"style" : HoleStyle.SIMPLE, "endStyle" : HoleEndStyle.BLIND, "holeDiameter" : 8 * mm, "holeDepth" : 12 * mm, "startFromSketch" : true, "locations" : qUnion([Q0]), "scope" : qUnion([Q1])});
        }
        {
            var Q0;
            Q0=makeQuery(id+"F1.opExtrude","SWEPT_FACE",FACE,{"disambiguationData":[OSD([sQuery(id+"F0.wireOp",EDGE,"E41.MirrorCS")])]});
            var sketch = newSketch(context, id + "F17", { "sketchPlane" : qUnion([Q0])});
            skPoint(sketch, "E91", {"position": v(80, 0.35) * mm});
            skLineSegment(sketch, "E92.bottom", {"start": v(75.5, -3.65) * mm, "end": v(84.5, -3.65) * mm});
            skLineSegment(sketch, "E92.top", {"start": v(75.5, 4.35) * mm, "end": v(84.5, 4.35) * mm});
            skLineSegment(sketch, "E92.left", {"start": v(75.5, -3.65) * mm, "end": v(75.5, 4.35) * mm});
            skLineSegment(sketch, "E92.right", {"start": v(84.5, -3.65) * mm, "end": v(84.5, 4.35) * mm});
            skSolve(sketch);
        }
        {
            var Q0;
            Q0=makeQuery(id+"F17.imprint","IMPRINT",FACE,{"disambiguationData":[TD([[makeQuery(id+"F17.imprint","IMPRINT",EDGE,{"derivedFrom":sQuery(id+"F17.wireOp",EDGE,"E92.bottom")}),1.0]])]});
            extrude(context, id + "F18", {"entities" : qUnion([Q0]), "operationType" : NewBodyOperationType.REMOVE, "oppositeDirection" : true, "depth" : 6 * mm});
        }
        {
            var Q0;
            Q0=makeQuery(id+"F1.opExtrude","SWEPT_FACE",FACE,{"disambiguationData":[OSD([sQuery(id+"F0.wireOp",EDGE,"E23.MirrorCS")])]});
            var sketch = newSketch(context, id + "F19", { "sketchPlane" : qUnion([Q0])});
            skLineSegment(sketch, "E93.bottom", {"start": v(-74.5, -4) * mm, "end": v(-65.5, -4) * mm});
            skLineSegment(sketch, "E93.top", {"start": v(-74.5, 4) * mm, "end": v(-65.5, 4) * mm});
            skLineSegment(sketch, "E93.left", {"start": v(-74.5, -4) * mm, "end": v(-74.5, 4) * mm});
            skLineSegment(sketch, "E93.right", {"start": v(-65.5, -4) * mm, "end": v(-65.5, 4) * mm});
            skPoint(sketch, "E93.middle", {"position": v(-70, 0) * mm});
            skPoint(sketch, "E93.middle.positionSnap0", {"position": v(-70, -17.5) * mm});
            skPoint(sketch, "E93.centerSnap0", {"position": v(-70, -17.5) * mm});
            skSolve(sketch);
        }
        {
            var Q0;
            Q0=makeQuery(id+"F19.imprint","IMPRINT",FACE,{"disambiguationData":[TD([[makeQuery(id+"F19.imprint","IMPRINT",EDGE,{"derivedFrom":sQuery(id+"F19.wireOp",EDGE,"E93.bottom")}),1.0]])]});
            extrude(context, id + "F20", {"entities" : qUnion([Q0]), "operationType" : NewBodyOperationType.REMOVE, "oppositeDirection" : true, "depth" : 6 * mm});
        }
        {
            var Q0;
            Q0=makeQuery(id+"F18.boolean.opBoolean","MERGE",FACE,{"derivedFrom":[makeQuery(id+"F1.opExtrude","SWEPT_FACE",FACE,{"disambiguationData":[OSD([sQuery(id+"F0.wireOp",EDGE,"E42.MirrorCS")])]}),makeQuery(id+"F1.opExtrude","SWEPT_FACE",FACE,{"disambiguationData":[OSD([sQuery(id+"F0.wireOp",EDGE,"E51.MirrorCS")])]}),makeQuery(id+"F18.opExtrude","CAP_FACE",FACE,{"disambiguationData":[OSD([sQuery(id+"F17.wireOp",EDGE,"E92.bottom"),sQuery(id+"F17.wireOp",EDGE,"E92.top"),sQuery(id+"F17.wireOp",EDGE,"E92.left"),sQuery(id+"F17.wireOp",EDGE,"E92.right")])],"isStart":false})]});
            var sketch = newSketch(context, id + "F21", { "sketchPlane" : qUnion([Q0])});
            skPoint(sketch, "E94", {"position": v(80, 0) * mm});
            skSolve(sketch);
        }
        {
            var Q0;
            Q0=makeQuery(id+"F20.boolean.opBoolean","MERGE",FACE,{"derivedFrom":[makeQuery(id+"F1.opExtrude","SWEPT_FACE",FACE,{"disambiguationData":[OSD([sQuery(id+"F0.wireOp",EDGE,"E24.MirrorCS")])]}),makeQuery(id+"F1.opExtrude","SWEPT_FACE",FACE,{"disambiguationData":[OSD([sQuery(id+"F0.wireOp",EDGE,"E29.MirrorCS")])]}),makeQuery(id+"F20.opExtrude","CAP_FACE",FACE,{"disambiguationData":[OSD([sQuery(id+"F19.wireOp",EDGE,"E93.bottom"),sQuery(id+"F19.wireOp",EDGE,"E93.top"),sQuery(id+"F19.wireOp",EDGE,"E93.left"),sQuery(id+"F19.wireOp",EDGE,"E93.right")])],"isStart":false})]});
            var sketch = newSketch(context, id + "F22", { "sketchPlane" : qUnion([Q0])});
            skPoint(sketch, "E95", {"position": v(-70, 0) * mm});
            skSolve(sketch);
        }
        {
            var Q0;
            Q0=sQuery(id+"F22.wireOp",VERTEX,"E95");
            var Q1;
            Q1=sQuery(id+"F21.wireOp",VERTEX,"E94");
            var Q2;
            Q2=makeQuery(id+"F1.opExtrude","SWEPT_BODY",BODY,{"disambiguationData":[OSD([sQuery(id+"F0.wireOp",EDGE,"E0.0"),sQuery(id+"F0.wireOp",EDGE,"E1.0"),sQuery(id+"F0.wireOp",EDGE,"E2.0"),sQuery(id+"F0.wireOp",EDGE,"E3.MirrorCS"),sQuery(id+"F0.wireOp",EDGE,"E4.MirrorCS"),sQuery(id+"F0.wireOp",EDGE,"E5.MirrorCS"),sQuery(id+"F0.wireOp",EDGE,"E6.trimOffspring"),sQuery(id+"F0.wireOp",EDGE,"E7.trimOffspring"),sQuery(id+"F0.wireOp",EDGE,"E8.trimOffspring"),sQuery(id+"F0.wireOp",EDGE,"E9.trimOffspring"),sQuery(id+"F0.wireOp",EDGE,"E10.trimOffspring"),sQuery(id+"F0.wireOp",EDGE,"E11.trimOffspring"),sQuery(id+"F0.wireOp",EDGE,"E12.trimOffspring"),sQuery(id+"F0.wireOp",EDGE,"E13.trimOffspring"),sQuery(id+"F0.wireOp",EDGE,"E16.MirrorCS"),sQuery(id+"F0.wireOp",EDGE,"E14.MirrorCS"),sQuery(id+"F0.wireOp",EDGE,"E15.MirrorCS"),sQuery(id+"F0.wireOp",EDGE,"E18.trimOffspring"),sQuery(id+"F0.wireOp",EDGE,"E19.trimOffspring"),sQuery(id+"F0.wireOp",EDGE,"E20"),sQuery(id+"F0.wireOp",EDGE,"E21.MirrorCS"),sQuery(id+"F0.wireOp",EDGE,"E22.MirrorCS"),sQuery(id+"F0.wireOp",EDGE,"E23.MirrorCS"),sQuery(id+"F0.wireOp",EDGE,"E24.MirrorCS"),sQuery(id+"F0.wireOp",EDGE,"E25.MirrorCS"),sQuery(id+"F0.wireOp",EDGE,"E26.MirrorCS"),sQuery(id+"F0.wireOp",EDGE,"E27.MirrorCS"),sQuery(id+"F0.wireOp",EDGE,"E28.MirrorCS"),sQuery(id+"F0.wireOp",EDGE,"E29.MirrorCS"),sQuery(id+"F0.wireOp",EDGE,"E30.MirrorCS"),sQuery(id+"F0.wireOp",EDGE,"E31.MirrorCS"),sQuery(id+"F0.wireOp",EDGE,"E32"),sQuery(id+"F0.wireOp",EDGE,"E33"),sQuery(id+"F0.wireOp",EDGE,"E39.MirrorCS"),sQuery(id+"F0.wireOp",EDGE,"E36.MirrorCS"),sQuery(id+"F0.wireOp",EDGE,"E34.MirrorCS"),sQuery(id+"F0.wireOp",EDGE,"E35.MirrorCS"),sQuery(id+"F0.wireOp",EDGE,"E38.MirrorCS"),sQuery(id+"F0.wireOp",EDGE,"E40"),sQuery(id+"F0.wireOp",EDGE,"E41.MirrorCS"),sQuery(id+"F0.wireOp",EDGE,"E42.MirrorCS"),sQuery(id+"F0.wireOp",EDGE,"E43.MirrorCS"),sQuery(id+"F0.wireOp",EDGE,"E44.MirrorCS"),sQuery(id+"F0.wireOp",EDGE,"E45.MirrorCS"),sQuery(id+"F0.wireOp",EDGE,"E46.MirrorCS"),sQuery(id+"F0.wireOp",EDGE,"E47.MirrorCS"),sQuery(id+"F0.wireOp",EDGE,"E48.MirrorCS"),sQuery(id+"F0.wireOp",EDGE,"E49.MirrorCS"),sQuery(id+"F0.wireOp",EDGE,"E50.MirrorCS"),sQuery(id+"F0.wireOp",EDGE,"E51.MirrorCS"),sQuery(id+"F0.wireOp",EDGE,"E54.MirrorCS"),sQuery(id+"F0.wireOp",EDGE,"E55.MirrorCS"),sQuery(id+"F0.wireOp",EDGE,"E59.MirrorCS"),sQuery(id+"F0.wireOp",EDGE,"E62.MirrorCS"),sQuery(id+"F0.wireOp",EDGE,"E61.MirrorCS"),sQuery(id+"F0.wireOp",EDGE,"E63.MirrorCS"),sQuery(id+"F0.wireOp",EDGE,"E56.MirrorCS"),sQuery(id+"F0.wireOp",EDGE,"E60.MirrorCS"),sQuery(id+"F0.wireOp",EDGE,"E64.MirrorCS"),sQuery(id+"F0.wireOp",EDGE,"E57.MirrorCS"),sQuery(id+"F0.wireOp",EDGE,"E65.MirrorCS"),sQuery(id+"F0.wireOp",EDGE,"E58.MirrorCS"),sQuery(id+"F0.wireOp",EDGE,"E66.MirrorCS"),sQuery(id+"F0.wireOp",EDGE,"E67.MirrorCS"),sQuery(id+"F0.wireOp",EDGE,"E68.MirrorCS"),sQuery(id+"F0.wireOp",EDGE,"E72.MirrorCS"),sQuery(id+"F0.wireOp",EDGE,"E71.MirrorCS"),sQuery(id+"F0.wireOp",EDGE,"E73.MirrorCS"),sQuery(id+"F0.wireOp",EDGE,"E80.MirrorCS"),sQuery(id+"F0.wireOp",EDGE,"E74.MirrorCS"),sQuery(id+"F0.wireOp",EDGE,"E81.MirrorCS"),sQuery(id+"F0.wireOp",EDGE,"E76.MirrorCS"),sQuery(id+"F0.wireOp",EDGE,"E78.MirrorCS"),sQuery(id+"F0.wireOp",EDGE,"E77.MirrorCS"),sQuery(id+"F0.wireOp",EDGE,"E75.MirrorCS"),sQuery(id+"F0.wireOp",EDGE,"E79.MirrorCS")])]});
            hole(context, id + "F23", {"style" : HoleStyle.SIMPLE, "endStyle" : HoleEndStyle.BLIND, "holeDiameter" : 8 * mm, "holeDepth" : 12 * mm, "startFromSketch" : true, "locations" : qUnion([Q0, Q1]), "scope" : qUnion([Q2])});
        }
        {
            var Q0;
            Q0=makeQuery(id+"F1.opExtrude","SWEPT_FACE",FACE,{"disambiguationData":[OSD([sQuery(id+"F0.wireOp",EDGE,"E34.MirrorCS")])]});
            var sketch = newSketch(context, id + "F24", { "sketchPlane" : qUnion([Q0])});
            skLineSegment(sketch, "E96", {"start": v(-73.25, 0) * mm, "end": v(-70.25, 0) * mm});
            skPoint(sketch, "E96.endSnap0", {"position": v(-73.25, 0) * mm});
            skLineSegment(sketch, "E97.bottom", {"start": v(-62.75, 7.5) * mm, "end": v(-77.75, 7.5) * mm});
            skLineSegment(sketch, "E97.top", {"start": v(-62.75, -7.5) * mm, "end": v(-77.75, -7.5) * mm});
            skLineSegment(sketch, "E97.left", {"start": v(-62.75, 7.5) * mm, "end": v(-62.75, -7.5) * mm});
            skLineSegment(sketch, "E97.right", {"start": v(-77.75, 7.5) * mm, "end": v(-77.75, -7.5) * mm});
            skPoint(sketch, "E97.middle", {"position": v(-70.25, 0) * mm});
            skSolve(sketch);
        }
        {
            var Q0;
            Q0=makeQuery(id+"F1.opExtrude","SWEPT_FACE",FACE,{"disambiguationData":[OSD([sQuery(id+"F0.wireOp",EDGE,"E71.MirrorCS")])]});
            var sketch = newSketch(context, id + "F25", { "sketchPlane" : qUnion([Q0])});
            skLineSegment(sketch, "E98", {"start": v(2.25, 0) * mm, "end": v(5.25, 0) * mm});
            skPoint(sketch, "E98.endSnap0", {"position": v(2.25, 0) * mm});
            skLineSegment(sketch, "E99.bottom", {"start": v(12.75, -7.5) * mm, "end": v(-2.25, -7.5) * mm});
            skLineSegment(sketch, "E99.top", {"start": v(12.75, 7.5) * mm, "end": v(-2.25, 7.5) * mm});
            skLineSegment(sketch, "E99.left", {"start": v(12.75, -7.5) * mm, "end": v(12.75, 7.5) * mm});
            skLineSegment(sketch, "E99.right", {"start": v(-2.25, -7.5) * mm, "end": v(-2.25, 7.5) * mm});
            skPoint(sketch, "E99.middle", {"position": v(5.25, 0) * mm});
            skSolve(sketch);
        }
        {
            var Q0;
            Q0=makeQuery(id+"F1.opExtrude","SWEPT_FACE",FACE,{"disambiguationData":[OSD([sQuery(id+"F0.wireOp",EDGE,"E55.MirrorCS")])]});
            var sketch = newSketch(context, id + "F26", { "sketchPlane" : qUnion([Q0])});
            skLineSegment(sketch, "E100", {"start": v(77.25, 0) * mm, "end": v(80.25, 0) * mm});
            skPoint(sketch, "E100.endSnap0", {"position": v(77.25, 0) * mm});
            skLineSegment(sketch, "E101.bottom", {"start": v(87.75, 7.5) * mm, "end": v(72.75, 7.5) * mm});
            skLineSegment(sketch, "E101.top", {"start": v(87.75, -7.5) * mm, "end": v(72.75, -7.5) * mm});
            skLineSegment(sketch, "E101.left", {"start": v(87.75, 7.5) * mm, "end": v(87.75, -7.5) * mm});
            skLineSegment(sketch, "E101.right", {"start": v(72.75, 7.5) * mm, "end": v(72.75, -7.5) * mm});
            skPoint(sketch, "E101.middle", {"position": v(80.25, 0) * mm});
            skSolve(sketch);
        }
        {
            var Q0;
            {var subQ0=sQuery(id+"F24.wireOp",EDGE,"E97.right");Q0=makeQuery(id+"F24.imprint","IMPRINT",FACE,{"disambiguationData":[TD([[makeQuery(id+"F24.imprint","IMPRINT",EDGE,{"derivedFrom":subQ0}),1.0]])]});}
            var Q1;
            {var subQ0=sQuery(id+"F24.wireOp",EDGE,"E97.left");Q1=makeQuery(id+"F24.imprint","IMPRINT",FACE,{"disambiguationData":[TD([[makeQuery(id+"F24.imprint","IMPRINT",EDGE,{"derivedFrom":subQ0}),-1.0]])]});}
            var Q2;
            {var subQ5=sQuery(id+"F25.wireOp",EDGE,"E99.right");Q2=makeQuery(id+"F25.imprint","IMPRINT",FACE,{"disambiguationData":[TD([[makeQuery(id+"F25.imprint","IMPRINT",EDGE,{"derivedFrom":subQ5}),1.0]])]});}
            var Q3;
            {var subQ0=sQuery(id+"F25.wireOp",EDGE,"E99.left");Q3=makeQuery(id+"F25.imprint","IMPRINT",FACE,{"disambiguationData":[TD([[makeQuery(id+"F25.imprint","IMPRINT",EDGE,{"derivedFrom":subQ0}),1.0]])]});}
            var Q4;
            {var subQ5=sQuery(id+"F26.wireOp",EDGE,"E101.right");Q4=makeQuery(id+"F26.imprint","IMPRINT",FACE,{"disambiguationData":[TD([[makeQuery(id+"F26.imprint","IMPRINT",EDGE,{"derivedFrom":subQ5}),1.0]])]});}
            var Q5;
            {var subQ4=sQuery(id+"F26.wireOp",EDGE,"E101.left");Q5=makeQuery(id+"F26.imprint","IMPRINT",FACE,{"disambiguationData":[TD([[makeQuery(id+"F26.imprint","IMPRINT",EDGE,{"derivedFrom":subQ4}),-1.0]])]});}
            extrude(context, id + "F27", {"entities" : qUnion([Q0, Q1, Q2, Q3, Q4, Q5]), "operationType" : NewBodyOperationType.REMOVE, "oppositeDirection" : true, "depth" : 8 * mm});
        }
        {
            var Q0;
            Q0=makeQuery(id+"F27.boolean.opBoolean","MERGE",FACE,{"derivedFrom":[makeQuery(id+"F1.opExtrude","SWEPT_FACE",FACE,{"disambiguationData":[OSD([sQuery(id+"F0.wireOp",EDGE,"E18.trimOffspring")])]}),makeQuery(id+"F1.opExtrude","SWEPT_FACE",FACE,{"disambiguationData":[OSD([sQuery(id+"F0.wireOp",EDGE,"E20")])]}),makeQuery(id+"F1.opExtrude","SWEPT_FACE",FACE,{"disambiguationData":[OSD([sQuery(id+"F0.wireOp",EDGE,"E39.MirrorCS")])]}),makeQuery(id+"F27.opExtrude","CAP_FACE",FACE,{"disambiguationData":[OSD([sQuery(id+"F24.wireOp",EDGE,"E97.bottom"),sQuery(id+"F24.wireOp",EDGE,"E97.top"),sQuery(id+"F24.wireOp",EDGE,"E97.left"),sQuery(id+"F24.wireOp",EDGE,"E97.right")])],"isStart":false})]});
            var sketch = newSketch(context, id + "F28", { "sketchPlane" : qUnion([Q0])});
            skPoint(sketch, "E102", {"position": v(-70.25, 0) * mm});
            skPoint(sketch, "E102.positionSnap0", {"position": v(-70.25, 17.5) * mm});
            skSolve(sketch);
        }
        {
            var Q0;
            Q0=makeQuery(id+"F27.boolean.opBoolean","MERGE",FACE,{"derivedFrom":[makeQuery(id+"F1.opExtrude","SWEPT_FACE",FACE,{"disambiguationData":[OSD([sQuery(id+"F0.wireOp",EDGE,"E73.MirrorCS")])]}),makeQuery(id+"F1.opExtrude","SWEPT_FACE",FACE,{"disambiguationData":[OSD([sQuery(id+"F0.wireOp",EDGE,"E80.MirrorCS")])]}),makeQuery(id+"F1.opExtrude","SWEPT_FACE",FACE,{"disambiguationData":[OSD([sQuery(id+"F0.wireOp",EDGE,"E81.MirrorCS")])]}),makeQuery(id+"F27.opExtrude","CAP_FACE",FACE,{"disambiguationData":[OSD([sQuery(id+"F25.wireOp",EDGE,"E99.bottom"),sQuery(id+"F25.wireOp",EDGE,"E99.top"),sQuery(id+"F25.wireOp",EDGE,"E99.left"),sQuery(id+"F25.wireOp",EDGE,"E99.right")])],"isStart":false})]});
            var sketch = newSketch(context, id + "F29", { "sketchPlane" : qUnion([Q0])});
            skPoint(sketch, "E103", {"position": v(5.25, 0) * mm});
            skSolve(sketch);
        }
        {
            var Q0;
            Q0=makeQuery(id+"F27.boolean.opBoolean","MERGE",FACE,{"derivedFrom":[makeQuery(id+"F1.opExtrude","SWEPT_FACE",FACE,{"disambiguationData":[OSD([sQuery(id+"F0.wireOp",EDGE,"E59.MirrorCS")])]}),makeQuery(id+"F1.opExtrude","SWEPT_FACE",FACE,{"disambiguationData":[OSD([sQuery(id+"F0.wireOp",EDGE,"E63.MirrorCS")])]}),makeQuery(id+"F1.opExtrude","SWEPT_FACE",FACE,{"disambiguationData":[OSD([sQuery(id+"F0.wireOp",EDGE,"E65.MirrorCS")])]}),makeQuery(id+"F27.opExtrude","CAP_FACE",FACE,{"disambiguationData":[OSD([sQuery(id+"F26.wireOp",EDGE,"E101.bottom"),sQuery(id+"F26.wireOp",EDGE,"E101.top"),sQuery(id+"F26.wireOp",EDGE,"E101.left"),sQuery(id+"F26.wireOp",EDGE,"E101.right")])],"isStart":false})]});
            var sketch = newSketch(context, id + "F30", { "sketchPlane" : qUnion([Q0])});
            skPoint(sketch, "E104", {"position": v(80.25, 0) * mm});
            skSolve(sketch);
        }
        {
            var Q0;
            Q0=sQuery(id+"F28.wireOp",VERTEX,"E102");
            var Q1;
            Q1=sQuery(id+"F29.wireOp",VERTEX,"E103");
            var Q2;
            Q2=sQuery(id+"F30.wireOp",VERTEX,"E104");
            var Q3;
            Q3=makeQuery(id+"F1.opExtrude","SWEPT_BODY",BODY,{"disambiguationData":[OSD([sQuery(id+"F0.wireOp",EDGE,"E0.0"),sQuery(id+"F0.wireOp",EDGE,"E1.0"),sQuery(id+"F0.wireOp",EDGE,"E2.0"),sQuery(id+"F0.wireOp",EDGE,"E3.MirrorCS"),sQuery(id+"F0.wireOp",EDGE,"E4.MirrorCS"),sQuery(id+"F0.wireOp",EDGE,"E5.MirrorCS"),sQuery(id+"F0.wireOp",EDGE,"E6.trimOffspring"),sQuery(id+"F0.wireOp",EDGE,"E7.trimOffspring"),sQuery(id+"F0.wireOp",EDGE,"E8.trimOffspring"),sQuery(id+"F0.wireOp",EDGE,"E9.trimOffspring"),sQuery(id+"F0.wireOp",EDGE,"E10.trimOffspring"),sQuery(id+"F0.wireOp",EDGE,"E11.trimOffspring"),sQuery(id+"F0.wireOp",EDGE,"E12.trimOffspring"),sQuery(id+"F0.wireOp",EDGE,"E13.trimOffspring"),sQuery(id+"F0.wireOp",EDGE,"E16.MirrorCS"),sQuery(id+"F0.wireOp",EDGE,"E14.MirrorCS"),sQuery(id+"F0.wireOp",EDGE,"E15.MirrorCS"),sQuery(id+"F0.wireOp",EDGE,"E18.trimOffspring"),sQuery(id+"F0.wireOp",EDGE,"E19.trimOffspring"),sQuery(id+"F0.wireOp",EDGE,"E20"),sQuery(id+"F0.wireOp",EDGE,"E21.MirrorCS"),sQuery(id+"F0.wireOp",EDGE,"E22.MirrorCS"),sQuery(id+"F0.wireOp",EDGE,"E23.MirrorCS"),sQuery(id+"F0.wireOp",EDGE,"E24.MirrorCS"),sQuery(id+"F0.wireOp",EDGE,"E25.MirrorCS"),sQuery(id+"F0.wireOp",EDGE,"E26.MirrorCS"),sQuery(id+"F0.wireOp",EDGE,"E27.MirrorCS"),sQuery(id+"F0.wireOp",EDGE,"E28.MirrorCS"),sQuery(id+"F0.wireOp",EDGE,"E29.MirrorCS"),sQuery(id+"F0.wireOp",EDGE,"E30.MirrorCS"),sQuery(id+"F0.wireOp",EDGE,"E31.MirrorCS"),sQuery(id+"F0.wireOp",EDGE,"E32"),sQuery(id+"F0.wireOp",EDGE,"E33"),sQuery(id+"F0.wireOp",EDGE,"E39.MirrorCS"),sQuery(id+"F0.wireOp",EDGE,"E36.MirrorCS"),sQuery(id+"F0.wireOp",EDGE,"E34.MirrorCS"),sQuery(id+"F0.wireOp",EDGE,"E35.MirrorCS"),sQuery(id+"F0.wireOp",EDGE,"E38.MirrorCS"),sQuery(id+"F0.wireOp",EDGE,"E40"),sQuery(id+"F0.wireOp",EDGE,"E41.MirrorCS"),sQuery(id+"F0.wireOp",EDGE,"E42.MirrorCS"),sQuery(id+"F0.wireOp",EDGE,"E43.MirrorCS"),sQuery(id+"F0.wireOp",EDGE,"E44.MirrorCS"),sQuery(id+"F0.wireOp",EDGE,"E45.MirrorCS"),sQuery(id+"F0.wireOp",EDGE,"E46.MirrorCS"),sQuery(id+"F0.wireOp",EDGE,"E47.MirrorCS"),sQuery(id+"F0.wireOp",EDGE,"E48.MirrorCS"),sQuery(id+"F0.wireOp",EDGE,"E49.MirrorCS"),sQuery(id+"F0.wireOp",EDGE,"E50.MirrorCS"),sQuery(id+"F0.wireOp",EDGE,"E51.MirrorCS"),sQuery(id+"F0.wireOp",EDGE,"E54.MirrorCS"),sQuery(id+"F0.wireOp",EDGE,"E55.MirrorCS"),sQuery(id+"F0.wireOp",EDGE,"E59.MirrorCS"),sQuery(id+"F0.wireOp",EDGE,"E62.MirrorCS"),sQuery(id+"F0.wireOp",EDGE,"E61.MirrorCS"),sQuery(id+"F0.wireOp",EDGE,"E63.MirrorCS"),sQuery(id+"F0.wireOp",EDGE,"E56.MirrorCS"),sQuery(id+"F0.wireOp",EDGE,"E60.MirrorCS"),sQuery(id+"F0.wireOp",EDGE,"E64.MirrorCS"),sQuery(id+"F0.wireOp",EDGE,"E57.MirrorCS"),sQuery(id+"F0.wireOp",EDGE,"E65.MirrorCS"),sQuery(id+"F0.wireOp",EDGE,"E58.MirrorCS"),sQuery(id+"F0.wireOp",EDGE,"E66.MirrorCS"),sQuery(id+"F0.wireOp",EDGE,"E67.MirrorCS"),sQuery(id+"F0.wireOp",EDGE,"E68.MirrorCS"),sQuery(id+"F0.wireOp",EDGE,"E72.MirrorCS"),sQuery(id+"F0.wireOp",EDGE,"E71.MirrorCS"),sQuery(id+"F0.wireOp",EDGE,"E73.MirrorCS"),sQuery(id+"F0.wireOp",EDGE,"E80.MirrorCS"),sQuery(id+"F0.wireOp",EDGE,"E74.MirrorCS"),sQuery(id+"F0.wireOp",EDGE,"E81.MirrorCS"),sQuery(id+"F0.wireOp",EDGE,"E76.MirrorCS"),sQuery(id+"F0.wireOp",EDGE,"E78.MirrorCS"),sQuery(id+"F0.wireOp",EDGE,"E77.MirrorCS"),sQuery(id+"F0.wireOp",EDGE,"E75.MirrorCS"),sQuery(id+"F0.wireOp",EDGE,"E79.MirrorCS")])]});
            hole(context, id + "F31", {"style" : HoleStyle.SIMPLE, "endStyle" : HoleEndStyle.BLIND, "holeDiameter" : 15 * mm, "holeDepth" : 5 * mm, "startFromSketch" : true, "locations" : qUnion([Q0, Q1, Q2]), "scope" : qUnion([Q3])});
        }
        {
            var Q0;
            Q0=makeQuery(id+"F1.opExtrude","CAP_EDGE",EDGE,{"disambiguationData":[OSD([sQuery(id+"F0.wireOp",EDGE,"E32")])],"isStart":false});
            var Q1;
            Q1=makeQuery(id+"F1.opExtrude","CAP_EDGE",EDGE,{"disambiguationData":[OSD([sQuery(id+"F0.wireOp",EDGE,"E32")])],"isStart":true});
            var Q2;
            Q2=makeQuery(id+"F1.opExtrude","CAP_EDGE",EDGE,{"disambiguationData":[OSD([sQuery(id+"F0.wireOp",EDGE,"E66.MirrorCS")])],"isStart":false});
            var Q3;
            Q3=makeQuery(id+"F1.opExtrude","CAP_EDGE",EDGE,{"disambiguationData":[OSD([sQuery(id+"F0.wireOp",EDGE,"E66.MirrorCS")])],"isStart":true});
            fillet(context, id + "F32", {"entities" : qUnion([Q0, Q1, Q2, Q3]), "radius" : 3 * mm, "tangentPropagation" : true, "allowEdgeOverflow" : false});
        }
        {
            var Q0;
            Q0=makeQuery(id+"F1.opExtrude","SWEPT_EDGE",EDGE,{"disambiguationData":[OSD([sQuery(id+"F0.wireOp",EDGE,"E56.MirrorCS"),sQuery(id+"F0.wireOp",EDGE,"E67.MirrorCS")])]});
            var Q1;
            Q1=makeQuery(id+"F1.opExtrude","SWEPT_EDGE",EDGE,{"disambiguationData":[OSD([sQuery(id+"F0.wireOp",EDGE,"E62.MirrorCS"),sQuery(id+"F0.wireOp",EDGE,"E64.MirrorCS")])]});
            var Q2;
            Q2=makeQuery(id+"F1.opExtrude","SWEPT_EDGE",EDGE,{"disambiguationData":[OSD([sQuery(id+"F0.wireOp",EDGE,"E64.MirrorCS"),sQuery(id+"F0.wireOp",EDGE,"E79.MirrorCS")])]});
            var Q3;
            Q3=makeQuery(id+"F1.opExtrude","SWEPT_EDGE",EDGE,{"disambiguationData":[OSD([sQuery(id+"F0.wireOp",EDGE,"E13.trimOffspring"),sQuery(id+"F0.wireOp",EDGE,"E74.MirrorCS")])]});
            var Q4;
            Q4=makeQuery(id+"F1.opExtrude","SWEPT_EDGE",EDGE,{"disambiguationData":[OSD([sQuery(id+"F0.wireOp",EDGE,"E13.trimOffspring"),sQuery(id+"F0.wireOp",EDGE,"E16.MirrorCS")])]});
            var Q5;
            Q5=makeQuery(id+"F1.opExtrude","SWEPT_EDGE",EDGE,{"disambiguationData":[OSD([sQuery(id+"F0.wireOp",EDGE,"E36.MirrorCS"),sQuery(id+"F0.wireOp",EDGE,"E40")])]});
            var Q6;
            {var subQ0=sQuery(id+"F0.wireOp",EDGE,"E38.MirrorCS");var subQ1=sQuery(id+"F0.wireOp",EDGE,"E34.MirrorCS");Q6=makeQuery(id+"F27.boolean.opBoolean","SPLIT",EDGE,{"disambiguationData":[TD([makeQuery(id+"F27.opExtrude","SWEPT_FACE",FACE,{"disambiguationData":[OSD([sQuery(id+"F24.wireOp",EDGE,"E97.top")])]})])],"derivedFrom":makeQuery(id+"F1.opExtrude","SWEPT_EDGE",EDGE,{"disambiguationData":[OSD([subQ1,subQ0])]})});}
            var Q7;
            {var subQ0=sQuery(id+"F0.wireOp",EDGE,"E35.MirrorCS");var subQ1=sQuery(id+"F0.wireOp",EDGE,"E34.MirrorCS");Q7=makeQuery(id+"F27.boolean.opBoolean","SPLIT",EDGE,{"disambiguationData":[TD([makeQuery(id+"F27.opExtrude","SWEPT_FACE",FACE,{"disambiguationData":[OSD([sQuery(id+"F24.wireOp",EDGE,"E97.top")])]})])],"derivedFrom":makeQuery(id+"F1.opExtrude","SWEPT_EDGE",EDGE,{"disambiguationData":[OSD([subQ1,subQ0])]})});}
            var Q8;
            {var subQ0=sQuery(id+"F0.wireOp",EDGE,"E19.trimOffspring");var subQ1=sQuery(id+"F0.wireOp",EDGE,"E15.MirrorCS");Q8=makeQuery(id+"F27.boolean.opBoolean","SPLIT",EDGE,{"disambiguationData":[TD([makeQuery(id+"F27.opExtrude","SWEPT_FACE",FACE,{"disambiguationData":[OSD([sQuery(id+"F24.wireOp",EDGE,"E97.top")])]})])],"derivedFrom":makeQuery(id+"F1.opExtrude","SWEPT_EDGE",EDGE,{"disambiguationData":[OSD([subQ1,subQ0])]})});}
            var Q9;
            {var subQ0=sQuery(id+"F0.wireOp",EDGE,"E19.trimOffspring");var subQ1=sQuery(id+"F0.wireOp",EDGE,"E14.MirrorCS");Q9=makeQuery(id+"F27.boolean.opBoolean","SPLIT",EDGE,{"disambiguationData":[TD([makeQuery(id+"F27.opExtrude","SWEPT_FACE",FACE,{"disambiguationData":[OSD([sQuery(id+"F24.wireOp",EDGE,"E97.top")])]})])],"derivedFrom":makeQuery(id+"F1.opExtrude","SWEPT_EDGE",EDGE,{"disambiguationData":[OSD([subQ1,subQ0])]})});}
            var Q10;
            {var subQ0=sQuery(id+"F0.wireOp",EDGE,"E19.trimOffspring");var subQ1=sQuery(id+"F0.wireOp",EDGE,"E14.MirrorCS");Q10=makeQuery(id+"F27.boolean.opBoolean","SPLIT",EDGE,{"disambiguationData":[TD([makeQuery(id+"F27.opExtrude","SWEPT_FACE",FACE,{"disambiguationData":[OSD([sQuery(id+"F24.wireOp",EDGE,"E97.bottom")])]})])],"derivedFrom":makeQuery(id+"F1.opExtrude","SWEPT_EDGE",EDGE,{"disambiguationData":[OSD([subQ1,subQ0])]})});}
            var Q11;
            {var subQ0=sQuery(id+"F0.wireOp",EDGE,"E19.trimOffspring");var subQ1=sQuery(id+"F0.wireOp",EDGE,"E15.MirrorCS");Q11=makeQuery(id+"F27.boolean.opBoolean","SPLIT",EDGE,{"disambiguationData":[TD([makeQuery(id+"F27.opExtrude","SWEPT_FACE",FACE,{"disambiguationData":[OSD([sQuery(id+"F24.wireOp",EDGE,"E97.bottom")])]})])],"derivedFrom":makeQuery(id+"F1.opExtrude","SWEPT_EDGE",EDGE,{"disambiguationData":[OSD([subQ1,subQ0])]})});}
            var Q12;
            {var subQ0=sQuery(id+"F0.wireOp",EDGE,"E35.MirrorCS");var subQ1=sQuery(id+"F0.wireOp",EDGE,"E34.MirrorCS");Q12=makeQuery(id+"F27.boolean.opBoolean","SPLIT",EDGE,{"disambiguationData":[TD([makeQuery(id+"F27.opExtrude","SWEPT_FACE",FACE,{"disambiguationData":[OSD([sQuery(id+"F24.wireOp",EDGE,"E97.bottom")])]})])],"derivedFrom":makeQuery(id+"F1.opExtrude","SWEPT_EDGE",EDGE,{"disambiguationData":[OSD([subQ1,subQ0])]})});}
            var Q13;
            {var subQ0=sQuery(id+"F0.wireOp",EDGE,"E38.MirrorCS");var subQ1=sQuery(id+"F0.wireOp",EDGE,"E34.MirrorCS");Q13=makeQuery(id+"F27.boolean.opBoolean","SPLIT",EDGE,{"disambiguationData":[TD([makeQuery(id+"F27.opExtrude","SWEPT_FACE",FACE,{"disambiguationData":[OSD([sQuery(id+"F24.wireOp",EDGE,"E97.bottom")])]})])],"derivedFrom":makeQuery(id+"F1.opExtrude","SWEPT_EDGE",EDGE,{"disambiguationData":[OSD([subQ1,subQ0])]})});}
            var Q14;
            {var subQ0=sQuery(id+"F0.wireOp",EDGE,"E78.MirrorCS");var subQ1=sQuery(id+"F0.wireOp",EDGE,"E71.MirrorCS");Q14=makeQuery(id+"F27.boolean.opBoolean","SPLIT",EDGE,{"disambiguationData":[TD([makeQuery(id+"F27.opExtrude","SWEPT_FACE",FACE,{"disambiguationData":[OSD([sQuery(id+"F25.wireOp",EDGE,"E99.bottom")])]})])],"derivedFrom":makeQuery(id+"F1.opExtrude","SWEPT_EDGE",EDGE,{"disambiguationData":[OSD([subQ1,subQ0])]})});}
            var Q15;
            {var subQ0=sQuery(id+"F0.wireOp",EDGE,"E76.MirrorCS");var subQ1=sQuery(id+"F0.wireOp",EDGE,"E71.MirrorCS");Q15=makeQuery(id+"F27.boolean.opBoolean","SPLIT",EDGE,{"disambiguationData":[TD([makeQuery(id+"F27.opExtrude","SWEPT_FACE",FACE,{"disambiguationData":[OSD([sQuery(id+"F25.wireOp",EDGE,"E99.bottom")])]})])],"derivedFrom":makeQuery(id+"F1.opExtrude","SWEPT_EDGE",EDGE,{"disambiguationData":[OSD([subQ1,subQ0])]})});}
            var Q16;
            {var subQ0=sQuery(id+"F0.wireOp",EDGE,"E75.MirrorCS");var subQ1=sQuery(id+"F0.wireOp",EDGE,"E72.MirrorCS");Q16=makeQuery(id+"F27.boolean.opBoolean","SPLIT",EDGE,{"disambiguationData":[TD([makeQuery(id+"F27.opExtrude","SWEPT_FACE",FACE,{"disambiguationData":[OSD([sQuery(id+"F25.wireOp",EDGE,"E99.bottom")])]})])],"derivedFrom":makeQuery(id+"F1.opExtrude","SWEPT_EDGE",EDGE,{"disambiguationData":[OSD([subQ1,subQ0])]})});}
            var Q17;
            {var subQ0=sQuery(id+"F0.wireOp",EDGE,"E77.MirrorCS");var subQ1=sQuery(id+"F0.wireOp",EDGE,"E72.MirrorCS");Q17=makeQuery(id+"F27.boolean.opBoolean","SPLIT",EDGE,{"disambiguationData":[TD([makeQuery(id+"F27.opExtrude","SWEPT_FACE",FACE,{"disambiguationData":[OSD([sQuery(id+"F25.wireOp",EDGE,"E99.bottom")])]})])],"derivedFrom":makeQuery(id+"F1.opExtrude","SWEPT_EDGE",EDGE,{"disambiguationData":[OSD([subQ1,subQ0])]})});}
            var Q18;
            {var subQ0=sQuery(id+"F0.wireOp",EDGE,"E75.MirrorCS");var subQ1=sQuery(id+"F0.wireOp",EDGE,"E72.MirrorCS");Q18=makeQuery(id+"F27.boolean.opBoolean","SPLIT",EDGE,{"disambiguationData":[TD([makeQuery(id+"F27.opExtrude","SWEPT_FACE",FACE,{"disambiguationData":[OSD([sQuery(id+"F25.wireOp",EDGE,"E99.top")])]})])],"derivedFrom":makeQuery(id+"F1.opExtrude","SWEPT_EDGE",EDGE,{"disambiguationData":[OSD([subQ1,subQ0])]})});}
            var Q19;
            {var subQ0=sQuery(id+"F0.wireOp",EDGE,"E76.MirrorCS");var subQ1=sQuery(id+"F0.wireOp",EDGE,"E71.MirrorCS");Q19=makeQuery(id+"F27.boolean.opBoolean","SPLIT",EDGE,{"disambiguationData":[TD([makeQuery(id+"F27.opExtrude","SWEPT_FACE",FACE,{"disambiguationData":[OSD([sQuery(id+"F25.wireOp",EDGE,"E99.top")])]})])],"derivedFrom":makeQuery(id+"F1.opExtrude","SWEPT_EDGE",EDGE,{"disambiguationData":[OSD([subQ1,subQ0])]})});}
            var Q20;
            {var subQ0=sQuery(id+"F0.wireOp",EDGE,"E78.MirrorCS");var subQ1=sQuery(id+"F0.wireOp",EDGE,"E71.MirrorCS");Q20=makeQuery(id+"F27.boolean.opBoolean","SPLIT",EDGE,{"disambiguationData":[TD([makeQuery(id+"F27.opExtrude","SWEPT_FACE",FACE,{"disambiguationData":[OSD([sQuery(id+"F25.wireOp",EDGE,"E99.top")])]})])],"derivedFrom":makeQuery(id+"F1.opExtrude","SWEPT_EDGE",EDGE,{"disambiguationData":[OSD([subQ1,subQ0])]})});}
            var Q21;
            {var subQ0=sQuery(id+"F0.wireOp",EDGE,"E78.MirrorCS");var subQ1=sQuery(id+"F0.wireOp",EDGE,"E71.MirrorCS");Q21=makeQuery(id+"F27.boolean.opBoolean","SPLIT",EDGE,{"disambiguationData":[TD([makeQuery(id+"F27.opExtrude","SWEPT_FACE",FACE,{"disambiguationData":[OSD([sQuery(id+"F25.wireOp",EDGE,"E99.top")])]})])],"derivedFrom":makeQuery(id+"F1.opExtrude","SWEPT_EDGE",EDGE,{"disambiguationData":[OSD([subQ1,subQ0])]})});}
            var Q22;
            {var subQ0=sQuery(id+"F0.wireOp",EDGE,"E60.MirrorCS");var subQ1=sQuery(id+"F0.wireOp",EDGE,"E55.MirrorCS");Q22=makeQuery(id+"F27.boolean.opBoolean","SPLIT",EDGE,{"disambiguationData":[TD([makeQuery(id+"F27.opExtrude","SWEPT_FACE",FACE,{"disambiguationData":[OSD([sQuery(id+"F26.wireOp",EDGE,"E101.bottom")])]})])],"derivedFrom":makeQuery(id+"F1.opExtrude","SWEPT_EDGE",EDGE,{"disambiguationData":[OSD([subQ1,subQ0])]})});}
            var Q23;
            {var subQ0=sQuery(id+"F0.wireOp",EDGE,"E58.MirrorCS");var subQ1=sQuery(id+"F0.wireOp",EDGE,"E55.MirrorCS");Q23=makeQuery(id+"F27.boolean.opBoolean","SPLIT",EDGE,{"disambiguationData":[TD([makeQuery(id+"F27.opExtrude","SWEPT_FACE",FACE,{"disambiguationData":[OSD([sQuery(id+"F26.wireOp",EDGE,"E101.bottom")])]})])],"derivedFrom":makeQuery(id+"F1.opExtrude","SWEPT_EDGE",EDGE,{"disambiguationData":[OSD([subQ1,subQ0])]})});}
            var Q24;
            {var subQ0=sQuery(id+"F0.wireOp",EDGE,"E61.MirrorCS");var subQ1=sQuery(id+"F0.wireOp",EDGE,"E54.MirrorCS");Q24=makeQuery(id+"F27.boolean.opBoolean","SPLIT",EDGE,{"disambiguationData":[TD([makeQuery(id+"F27.opExtrude","SWEPT_FACE",FACE,{"disambiguationData":[OSD([sQuery(id+"F26.wireOp",EDGE,"E101.bottom")])]})])],"derivedFrom":makeQuery(id+"F1.opExtrude","SWEPT_EDGE",EDGE,{"disambiguationData":[OSD([subQ1,subQ0])]})});}
            var Q25;
            {var subQ0=sQuery(id+"F0.wireOp",EDGE,"E57.MirrorCS");var subQ1=sQuery(id+"F0.wireOp",EDGE,"E54.MirrorCS");Q25=makeQuery(id+"F27.boolean.opBoolean","SPLIT",EDGE,{"disambiguationData":[TD([makeQuery(id+"F27.opExtrude","SWEPT_FACE",FACE,{"disambiguationData":[OSD([sQuery(id+"F26.wireOp",EDGE,"E101.bottom")])]})])],"derivedFrom":makeQuery(id+"F1.opExtrude","SWEPT_EDGE",EDGE,{"disambiguationData":[OSD([subQ1,subQ0])]})});}
            var Q26;
            {var subQ0=sQuery(id+"F0.wireOp",EDGE,"E57.MirrorCS");var subQ1=sQuery(id+"F0.wireOp",EDGE,"E54.MirrorCS");Q26=makeQuery(id+"F27.boolean.opBoolean","SPLIT",EDGE,{"disambiguationData":[TD([makeQuery(id+"F27.opExtrude","SWEPT_FACE",FACE,{"disambiguationData":[OSD([sQuery(id+"F26.wireOp",EDGE,"E101.top")])]})])],"derivedFrom":makeQuery(id+"F1.opExtrude","SWEPT_EDGE",EDGE,{"disambiguationData":[OSD([subQ1,subQ0])]})});}
            var Q27;
            {var subQ0=sQuery(id+"F0.wireOp",EDGE,"E61.MirrorCS");var subQ1=sQuery(id+"F0.wireOp",EDGE,"E54.MirrorCS");Q27=makeQuery(id+"F27.boolean.opBoolean","SPLIT",EDGE,{"disambiguationData":[TD([makeQuery(id+"F27.opExtrude","SWEPT_FACE",FACE,{"disambiguationData":[OSD([sQuery(id+"F26.wireOp",EDGE,"E101.top")])]})])],"derivedFrom":makeQuery(id+"F1.opExtrude","SWEPT_EDGE",EDGE,{"disambiguationData":[OSD([subQ1,subQ0])]})});}
            var Q28;
            {var subQ0=sQuery(id+"F0.wireOp",EDGE,"E58.MirrorCS");var subQ1=sQuery(id+"F0.wireOp",EDGE,"E55.MirrorCS");Q28=makeQuery(id+"F27.boolean.opBoolean","SPLIT",EDGE,{"disambiguationData":[TD([makeQuery(id+"F27.opExtrude","SWEPT_FACE",FACE,{"disambiguationData":[OSD([sQuery(id+"F26.wireOp",EDGE,"E101.top")])]})])],"derivedFrom":makeQuery(id+"F1.opExtrude","SWEPT_EDGE",EDGE,{"disambiguationData":[OSD([subQ1,subQ0])]})});}
            var Q29;
            {var subQ0=sQuery(id+"F0.wireOp",EDGE,"E60.MirrorCS");var subQ1=sQuery(id+"F0.wireOp",EDGE,"E55.MirrorCS");Q29=makeQuery(id+"F27.boolean.opBoolean","SPLIT",EDGE,{"disambiguationData":[TD([makeQuery(id+"F27.opExtrude","SWEPT_FACE",FACE,{"disambiguationData":[OSD([sQuery(id+"F26.wireOp",EDGE,"E101.top")])]})])],"derivedFrom":makeQuery(id+"F1.opExtrude","SWEPT_EDGE",EDGE,{"disambiguationData":[OSD([subQ1,subQ0])]})});}
            var Q30;
            {var subQ0=sQuery(id+"F0.wireOp",EDGE,"E77.MirrorCS");var subQ1=sQuery(id+"F0.wireOp",EDGE,"E72.MirrorCS");Q30=makeQuery(id+"F27.boolean.opBoolean","SPLIT",EDGE,{"disambiguationData":[TD([makeQuery(id+"F27.opExtrude","SWEPT_FACE",FACE,{"disambiguationData":[OSD([sQuery(id+"F25.wireOp",EDGE,"E99.top")])]})])],"derivedFrom":makeQuery(id+"F1.opExtrude","SWEPT_EDGE",EDGE,{"disambiguationData":[OSD([subQ1,subQ0])]})});}
            var Q31;
            Q31=makeQuery(id+"F1.opExtrude","SWEPT_EDGE",EDGE,{"disambiguationData":[OSD([sQuery(id+"F0.wireOp",EDGE,"E2.0"),sQuery(id+"F0.wireOp",EDGE,"E6.trimOffspring")])]});
            var Q32;
            Q32=makeQuery(id+"F1.opExtrude","SWEPT_EDGE",EDGE,{"disambiguationData":[OSD([sQuery(id+"F0.wireOp",EDGE,"E12.trimOffspring"),sQuery(id+"F0.wireOp",EDGE,"E50.MirrorCS")])]});
            var Q33;
            Q33=makeQuery(id+"F1.opExtrude","SWEPT_EDGE",EDGE,{"disambiguationData":[OSD([sQuery(id+"F0.wireOp",EDGE,"E3.MirrorCS"),sQuery(id+"F0.wireOp",EDGE,"E12.trimOffspring")])]});
            var Q34;
            Q34=makeQuery(id+"F1.opExtrude","SWEPT_EDGE",EDGE,{"disambiguationData":[OSD([sQuery(id+"F0.wireOp",EDGE,"E6.trimOffspring"),sQuery(id+"F0.wireOp",EDGE,"E22.MirrorCS")])]});
            var Q35;
            {var subQ0=sQuery(id+"F0.wireOp",EDGE,"E25.MirrorCS");var subQ1=sQuery(id+"F0.wireOp",EDGE,"E23.MirrorCS");Q35=makeQuery(id+"F20.boolean.opBoolean","SPLIT",EDGE,{"disambiguationData":[TD([makeQuery(id+"F20.opExtrude","SWEPT_FACE",FACE,{"disambiguationData":[OSD([sQuery(id+"F19.wireOp",EDGE,"E93.top")])]})])],"derivedFrom":makeQuery(id+"F1.opExtrude","SWEPT_EDGE",EDGE,{"disambiguationData":[OSD([subQ1,subQ0])]})});}
            var Q36;
            {var subQ0=sQuery(id+"F0.wireOp",EDGE,"E25.MirrorCS");var subQ1=sQuery(id+"F0.wireOp",EDGE,"E23.MirrorCS");Q36=makeQuery(id+"F20.boolean.opBoolean","SPLIT",EDGE,{"disambiguationData":[TD([makeQuery(id+"F20.opExtrude","SWEPT_FACE",FACE,{"disambiguationData":[OSD([sQuery(id+"F19.wireOp",EDGE,"E93.bottom")])]})])],"derivedFrom":makeQuery(id+"F1.opExtrude","SWEPT_EDGE",EDGE,{"disambiguationData":[OSD([subQ1,subQ0])]})});}
            var Q37;
            {var subQ0=sQuery(id+"F0.wireOp",EDGE,"E27.MirrorCS");var subQ1=sQuery(id+"F0.wireOp",EDGE,"E23.MirrorCS");Q37=makeQuery(id+"F20.boolean.opBoolean","SPLIT",EDGE,{"disambiguationData":[TD([makeQuery(id+"F20.opExtrude","SWEPT_FACE",FACE,{"disambiguationData":[OSD([sQuery(id+"F19.wireOp",EDGE,"E93.bottom")])]})])],"derivedFrom":makeQuery(id+"F1.opExtrude","SWEPT_EDGE",EDGE,{"disambiguationData":[OSD([subQ1,subQ0])]})});}
            var Q38;
            {var subQ0=sQuery(id+"F0.wireOp",EDGE,"E27.MirrorCS");var subQ1=sQuery(id+"F0.wireOp",EDGE,"E23.MirrorCS");Q38=makeQuery(id+"F20.boolean.opBoolean","SPLIT",EDGE,{"disambiguationData":[TD([makeQuery(id+"F20.opExtrude","SWEPT_FACE",FACE,{"disambiguationData":[OSD([sQuery(id+"F19.wireOp",EDGE,"E93.top")])]})])],"derivedFrom":makeQuery(id+"F1.opExtrude","SWEPT_EDGE",EDGE,{"disambiguationData":[OSD([subQ1,subQ0])]})});}
            var Q39;
            Q39=makeQuery(id+"F1.opExtrude","SWEPT_EDGE",EDGE,{"disambiguationData":[OSD([sQuery(id+"F0.wireOp",EDGE,"E28.MirrorCS"),sQuery(id+"F0.wireOp",EDGE,"E30.MirrorCS")])]});
            var Q40;
            Q40=makeQuery(id+"F1.opExtrude","SWEPT_EDGE",EDGE,{"disambiguationData":[OSD([sQuery(id+"F0.wireOp",EDGE,"E26.MirrorCS"),sQuery(id+"F0.wireOp",EDGE,"E33")])]});
            var Q41;
            Q41=makeQuery(id+"F1.opExtrude","SWEPT_EDGE",EDGE,{"disambiguationData":[OSD([sQuery(id+"F0.wireOp",EDGE,"E1.0"),sQuery(id+"F0.wireOp",EDGE,"E10.trimOffspring")])]});
            var Q42;
            {var subQ0=sQuery(id+"F0.wireOp",EDGE,"E0.0");var subQ1=sQuery(id+"F0.wireOp",EDGE,"E7.trimOffspring");Q42=makeQuery(id+"F14.boolean.opBoolean","SPLIT",EDGE,{"disambiguationData":[TD([makeQuery(id+"F14.opExtrude","SWEPT_FACE",FACE,{"disambiguationData":[OSD([sQuery(id+"F13.wireOp",EDGE,"E89.top")])]})])],"derivedFrom":makeQuery(id+"F1.opExtrude","SWEPT_EDGE",EDGE,{"disambiguationData":[OSD([subQ0,subQ1])]})});}
            var Q43;
            {var subQ0=sQuery(id+"F0.wireOp",EDGE,"E0.0");var subQ1=sQuery(id+"F0.wireOp",EDGE,"E7.trimOffspring");Q43=makeQuery(id+"F14.boolean.opBoolean","SPLIT",EDGE,{"disambiguationData":[TD([makeQuery(id+"F14.opExtrude","SWEPT_FACE",FACE,{"disambiguationData":[OSD([sQuery(id+"F13.wireOp",EDGE,"E89.bottom")])]})])],"derivedFrom":makeQuery(id+"F1.opExtrude","SWEPT_EDGE",EDGE,{"disambiguationData":[OSD([subQ0,subQ1])]})});}
            var Q44;
            {var subQ0=sQuery(id+"F0.wireOp",EDGE,"E7.trimOffspring");var subQ1=sQuery(id+"F0.wireOp",EDGE,"E4.MirrorCS");Q44=makeQuery(id+"F14.boolean.opBoolean","SPLIT",EDGE,{"disambiguationData":[TD([makeQuery(id+"F14.opExtrude","SWEPT_FACE",FACE,{"disambiguationData":[OSD([sQuery(id+"F13.wireOp",EDGE,"E89.bottom")])]})])],"derivedFrom":makeQuery(id+"F1.opExtrude","SWEPT_EDGE",EDGE,{"disambiguationData":[OSD([subQ1,subQ0])]})});}
            var Q45;
            {var subQ0=sQuery(id+"F0.wireOp",EDGE,"E7.trimOffspring");var subQ1=sQuery(id+"F0.wireOp",EDGE,"E4.MirrorCS");Q45=makeQuery(id+"F14.boolean.opBoolean","SPLIT",EDGE,{"disambiguationData":[TD([makeQuery(id+"F14.opExtrude","SWEPT_FACE",FACE,{"disambiguationData":[OSD([sQuery(id+"F13.wireOp",EDGE,"E89.top")])]})])],"derivedFrom":makeQuery(id+"F1.opExtrude","SWEPT_EDGE",EDGE,{"disambiguationData":[OSD([subQ1,subQ0])]})});}
            var Q46;
            Q46=makeQuery(id+"F1.opExtrude","SWEPT_EDGE",EDGE,{"disambiguationData":[OSD([sQuery(id+"F0.wireOp",EDGE,"E5.MirrorCS"),sQuery(id+"F0.wireOp",EDGE,"E8.trimOffspring")])]});
            var Q47;
            Q47=makeQuery(id+"F1.opExtrude","SWEPT_EDGE",EDGE,{"disambiguationData":[OSD([sQuery(id+"F0.wireOp",EDGE,"E46.MirrorCS"),sQuery(id+"F0.wireOp",EDGE,"E48.MirrorCS")])]});
            var Q48;
            {var subQ0=sQuery(id+"F0.wireOp",EDGE,"E45.MirrorCS");var subQ1=sQuery(id+"F0.wireOp",EDGE,"E41.MirrorCS");Q48=makeQuery(id+"F18.boolean.opBoolean","SPLIT",EDGE,{"disambiguationData":[TD([makeQuery(id+"F18.opExtrude","SWEPT_FACE",FACE,{"disambiguationData":[OSD([sQuery(id+"F17.wireOp",EDGE,"E92.bottom")])]})])],"derivedFrom":makeQuery(id+"F1.opExtrude","SWEPT_EDGE",EDGE,{"disambiguationData":[OSD([subQ1,subQ0])]})});}
            var Q49;
            {var subQ0=sQuery(id+"F0.wireOp",EDGE,"E47.MirrorCS");var subQ1=sQuery(id+"F0.wireOp",EDGE,"E41.MirrorCS");Q49=makeQuery(id+"F18.boolean.opBoolean","SPLIT",EDGE,{"disambiguationData":[TD([makeQuery(id+"F18.opExtrude","SWEPT_FACE",FACE,{"disambiguationData":[OSD([sQuery(id+"F17.wireOp",EDGE,"E92.bottom")])]})])],"derivedFrom":makeQuery(id+"F1.opExtrude","SWEPT_EDGE",EDGE,{"disambiguationData":[OSD([subQ1,subQ0])]})});}
            var Q50;
            {var subQ0=sQuery(id+"F0.wireOp",EDGE,"E45.MirrorCS");var subQ1=sQuery(id+"F0.wireOp",EDGE,"E41.MirrorCS");Q50=makeQuery(id+"F18.boolean.opBoolean","SPLIT",EDGE,{"disambiguationData":[TD([makeQuery(id+"F18.opExtrude","SWEPT_FACE",FACE,{"disambiguationData":[OSD([sQuery(id+"F17.wireOp",EDGE,"E92.top")])]})])],"derivedFrom":makeQuery(id+"F1.opExtrude","SWEPT_EDGE",EDGE,{"disambiguationData":[OSD([subQ1,subQ0])]})});}
            var Q51;
            {var subQ0=sQuery(id+"F0.wireOp",EDGE,"E47.MirrorCS");var subQ1=sQuery(id+"F0.wireOp",EDGE,"E41.MirrorCS");Q51=makeQuery(id+"F18.boolean.opBoolean","SPLIT",EDGE,{"disambiguationData":[TD([makeQuery(id+"F18.opExtrude","SWEPT_FACE",FACE,{"disambiguationData":[OSD([sQuery(id+"F17.wireOp",EDGE,"E92.top")])]})])],"derivedFrom":makeQuery(id+"F1.opExtrude","SWEPT_EDGE",EDGE,{"disambiguationData":[OSD([subQ1,subQ0])]})});}
            var Q52;
            Q52=makeQuery(id+"F1.opExtrude","SWEPT_EDGE",EDGE,{"disambiguationData":[OSD([sQuery(id+"F0.wireOp",EDGE,"E43.MirrorCS"),sQuery(id+"F0.wireOp",EDGE,"E68.MirrorCS")])]});
            var Q53;
            Q53=makeQuery(id+"F1.opExtrude","SWEPT_EDGE",EDGE,{"disambiguationData":[OSD([sQuery(id+"F0.wireOp",EDGE,"E44.MirrorCS"),sQuery(id+"F0.wireOp",EDGE,"E49.MirrorCS")])]});
            var Q54;
            Q54=makeQuery(id+"F1.opExtrude","SWEPT_EDGE",EDGE,{"disambiguationData":[OSD([sQuery(id+"F0.wireOp",EDGE,"E21.MirrorCS"),sQuery(id+"F0.wireOp",EDGE,"E31.MirrorCS")])]});
            fillet(context, id + "F33", {"entities" : qUnion([Q0, Q1, Q2, Q3, Q4, Q5, Q6, Q7, Q8, Q9, Q10, Q11, Q12, Q13, Q14, Q15, Q16, Q17, Q18, Q19, Q20, Q21, Q22, Q23, Q24, Q25, Q26, Q27, Q28, Q29, Q30, Q31, Q32, Q33, Q34, Q35, Q36, Q37, Q38, Q39, Q40, Q41, Q42, Q43, Q44, Q45, Q46, Q47, Q48, Q49, Q50, Q51, Q52, Q53, Q54]), "radius" : 1.5 * mm, "tangentPropagation" : true, "allowEdgeOverflow" : false});
        }
    });
